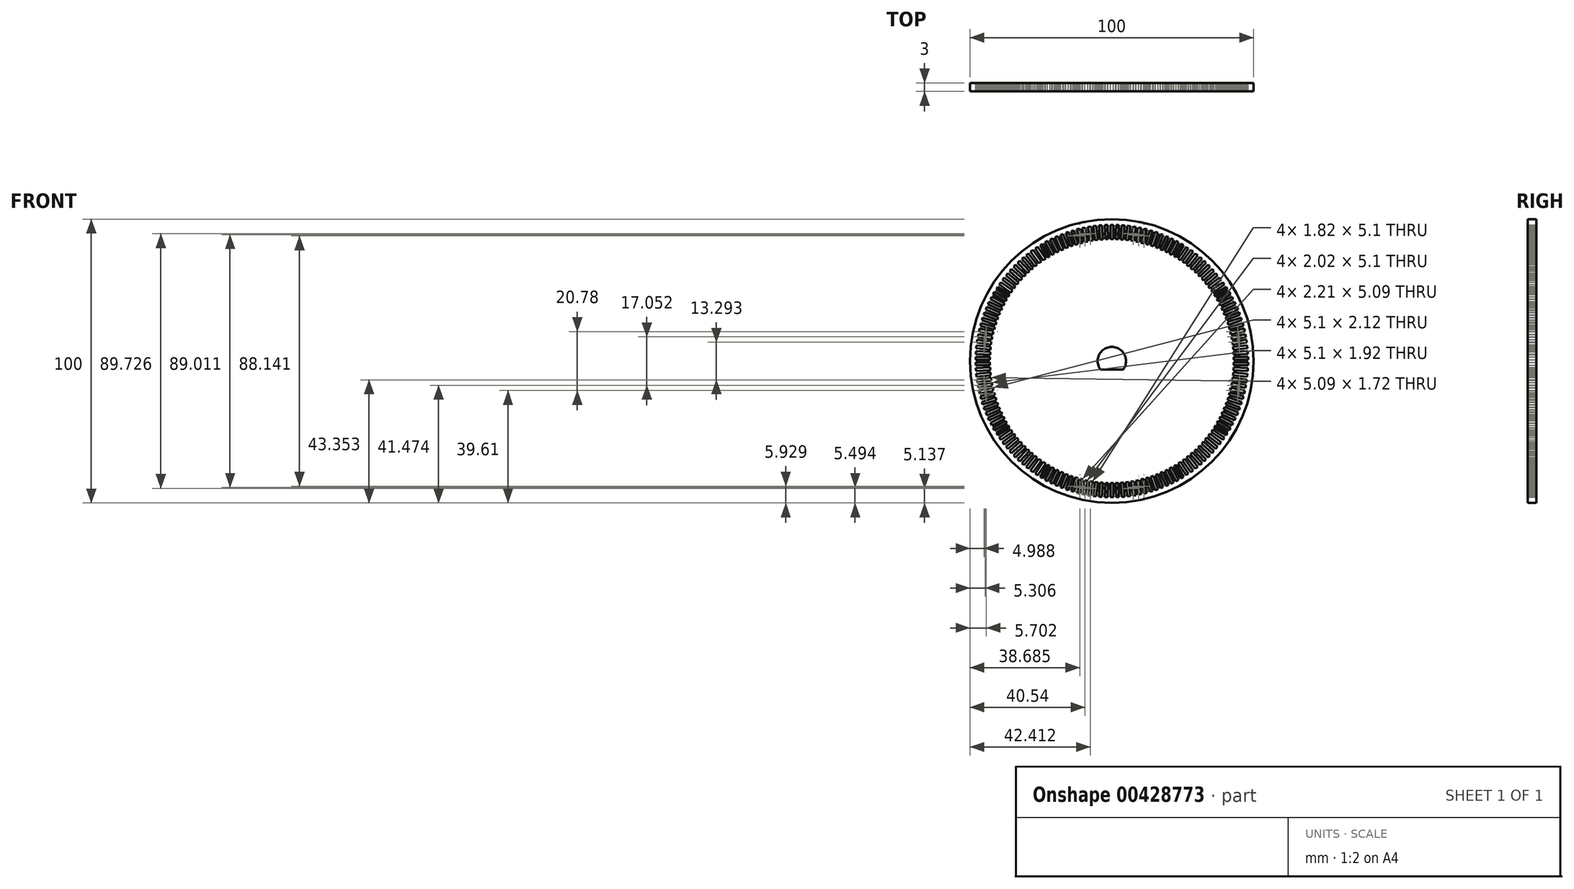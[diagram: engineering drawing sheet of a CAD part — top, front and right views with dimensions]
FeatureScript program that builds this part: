
annotation { "Feature Type Name" : "Feature", "Feature Type Description" : "" }
export const myFeature = defineFeature(function(context is Context, id is Id, definition is map)
    precondition{}
    {
        {
            var Q0;
            Q0=qCreatedBy(makeId("Front.planeOp"),FACE);
            var sketch = newSketch(context, id + "F0", { "sketchPlane" : qUnion([Q0])});
            skCircle(sketch, "E0", {"center": v(0, 0) * mm, "radius": 50 * mm});
            skLineSegment(sketch, "E1", {"start": v(0, 0) * mm, "end": v(0, 43) * mm});
            skLineSegment(sketch, "E2", {"start": v(0, 43) * mm, "end": v(0, 45.5) * mm});
            skLineSegment(sketch, "E3.bottom", {"start": v(0.5, 43) * mm, "end": v(-0.5, 43) * mm});
            skLineSegment(sketch, "E3.top", {"start": v(0.5, 48) * mm, "end": v(-0.5, 48) * mm});
            skLineSegment(sketch, "E3.left", {"start": v(0.5, 43) * mm, "end": v(0.5, 48) * mm});
            skLineSegment(sketch, "E3.right", {"start": v(-0.5, 43) * mm, "end": v(-0.5, 48) * mm});
            skPoint(sketch, "E3.middle", {"position": v(0, 45.5) * mm});
            skLineSegment(sketch, "E4.1.0", {"start": v(-2.3, 42.94) * mm, "end": v(-2.5, 47.94) * mm});
            skLineSegment(sketch, "E4.1.1", {"start": v(-1.3, 42.98) * mm, "end": v(-1.51, 47.98) * mm});
            skLineSegment(sketch, "E4.1.2", {"start": v(-1.8, 42.96) * mm, "end": v(-1.9, 45.46) * mm});
            skPoint(sketch, "E4.1.3", {"position": v(-1.9, 45.46) * mm});
            skLineSegment(sketch, "E4.1.4", {"start": v(-1.51, 47.98) * mm, "end": v(-2.5, 47.94) * mm});
            skLineSegment(sketch, "E4.1.5", {"start": v(-1.3, 42.98) * mm, "end": v(-2.3, 42.94) * mm});
            skLineSegment(sketch, "E4.2.0", {"start": v(-4.1, 42.8) * mm, "end": v(-4.51, 47.79) * mm});
            skLineSegment(sketch, "E4.2.1", {"start": v(-3.1, 42.9) * mm, "end": v(-3.52, 47.87) * mm});
            skLineSegment(sketch, "E4.2.2", {"start": v(-3.6, 42.85) * mm, "end": v(-3.8, 45.34) * mm});
            skPoint(sketch, "E4.2.3", {"position": v(-3.8, 45.34) * mm});
            skLineSegment(sketch, "E4.2.4", {"start": v(-3.52, 47.87) * mm, "end": v(-4.51, 47.79) * mm});
            skLineSegment(sketch, "E4.2.5", {"start": v(-3.1, 42.9) * mm, "end": v(-4.1, 42.8) * mm});
            skLineSegment(sketch, "E4.3.0", {"start": v(-5.89, 42.6) * mm, "end": v(-6.51, 47.56) * mm});
            skLineSegment(sketch, "E4.3.1", {"start": v(-4.9, 42.72) * mm, "end": v(-5.52, 47.68) * mm});
            skLineSegment(sketch, "E4.3.2", {"start": v(-5.39, 42.66) * mm, "end": v(-5.7, 45.14) * mm});
            skPoint(sketch, "E4.3.3", {"position": v(-5.7, 45.14) * mm});
            skLineSegment(sketch, "E4.3.4", {"start": v(-5.52, 47.68) * mm, "end": v(-6.51, 47.56) * mm});
            skLineSegment(sketch, "E4.3.5", {"start": v(-4.9, 42.72) * mm, "end": v(-5.89, 42.6) * mm});
            skLineSegment(sketch, "E4.4.0", {"start": v(-7.66, 42.31) * mm, "end": v(-8.5, 47.24) * mm});
            skLineSegment(sketch, "E4.4.1", {"start": v(-6.68, 42.48) * mm, "end": v(-7.51, 47.41) * mm});
            skLineSegment(sketch, "E4.4.2", {"start": v(-7.17, 42.4) * mm, "end": v(-7.59, 44.86) * mm});
            skPoint(sketch, "E4.4.3", {"position": v(-7.59, 44.86) * mm});
            skLineSegment(sketch, "E4.4.4", {"start": v(-7.51, 47.41) * mm, "end": v(-8.5, 47.24) * mm});
            skLineSegment(sketch, "E4.4.5", {"start": v(-6.68, 42.48) * mm, "end": v(-7.66, 42.31) * mm});
            skLineSegment(sketch, "E4.5.0", {"start": v(-9.43, 41.96) * mm, "end": v(-10.47, 46.85) * mm});
            skLineSegment(sketch, "E4.5.1", {"start": v(-8.45, 42.16) * mm, "end": v(-9.5, 47.06) * mm});
            skLineSegment(sketch, "E4.5.2", {"start": v(-8.94, 42.06) * mm, "end": v(-9.46, 44.5) * mm});
            skPoint(sketch, "E4.5.3", {"position": v(-9.46, 44.5) * mm});
            skLineSegment(sketch, "E4.5.4", {"start": v(-9.5, 47.06) * mm, "end": v(-10.47, 46.85) * mm});
            skLineSegment(sketch, "E4.5.5", {"start": v(-8.45, 42.16) * mm, "end": v(-9.43, 41.96) * mm});
            skLineSegment(sketch, "E4.6.0", {"start": v(-11.18, 41.52) * mm, "end": v(-12.42, 46.37) * mm});
            skLineSegment(sketch, "E4.6.1", {"start": v(-10.2, 41.77) * mm, "end": v(-11.45, 46.62) * mm});
            skLineSegment(sketch, "E4.6.2", {"start": v(-10.7, 41.65) * mm, "end": v(-11.32, 44.07) * mm});
            skPoint(sketch, "E4.6.3", {"position": v(-11.32, 44.07) * mm});
            skLineSegment(sketch, "E4.6.4", {"start": v(-11.45, 46.62) * mm, "end": v(-12.42, 46.37) * mm});
            skLineSegment(sketch, "E4.6.5", {"start": v(-10.2, 41.77) * mm, "end": v(-11.18, 41.52) * mm});
            skLineSegment(sketch, "E4.7.0", {"start": v(-12.9, 41.02) * mm, "end": v(-14.35, 45.8) * mm});
            skLineSegment(sketch, "E4.7.1", {"start": v(-11.95, 41.3) * mm, "end": v(-13.4, 46.1) * mm});
            skLineSegment(sketch, "E4.7.2", {"start": v(-12.43, 41.16) * mm, "end": v(-13.15, 43.56) * mm});
            skPoint(sketch, "E4.7.3", {"position": v(-13.15, 43.56) * mm});
            skLineSegment(sketch, "E4.7.4", {"start": v(-13.4, 46.1) * mm, "end": v(-14.35, 45.8) * mm});
            skLineSegment(sketch, "E4.7.5", {"start": v(-11.95, 41.3) * mm, "end": v(-12.9, 41.02) * mm});
            skLineSegment(sketch, "E4.8.0", {"start": v(-14.61, 40.44) * mm, "end": v(-16.26, 45.17) * mm});
            skLineSegment(sketch, "E4.8.1", {"start": v(-13.67, 40.77) * mm, "end": v(-15.31, 45.5) * mm});
            skLineSegment(sketch, "E4.8.2", {"start": v(-14.14, 40.6) * mm, "end": v(-14.96, 42.97) * mm});
            skPoint(sketch, "E4.8.3", {"position": v(-14.96, 42.97) * mm});
            skLineSegment(sketch, "E4.8.4", {"start": v(-15.31, 45.5) * mm, "end": v(-16.26, 45.17) * mm});
            skLineSegment(sketch, "E4.8.5", {"start": v(-13.67, 40.77) * mm, "end": v(-14.61, 40.44) * mm});
            skLineSegment(sketch, "E4.9.0", {"start": v(-16.3, 39.8) * mm, "end": v(-18.13, 44.45) * mm});
            skLineSegment(sketch, "E4.9.1", {"start": v(-15.36, 40.16) * mm, "end": v(-17.2, 44.81) * mm});
            skLineSegment(sketch, "E4.9.2", {"start": v(-15.83, 39.98) * mm, "end": v(-16.75, 42.3) * mm});
            skPoint(sketch, "E4.9.3", {"position": v(-16.75, 42.3) * mm});
            skLineSegment(sketch, "E4.9.4", {"start": v(-17.2, 44.81) * mm, "end": v(-18.13, 44.45) * mm});
            skLineSegment(sketch, "E4.9.5", {"start": v(-15.36, 40.16) * mm, "end": v(-16.3, 39.8) * mm});
            skLineSegment(sketch, "E4.10.0", {"start": v(-17.95, 39.08) * mm, "end": v(-19.98, 43.65) * mm});
            skLineSegment(sketch, "E4.10.1", {"start": v(-17.03, 39.49) * mm, "end": v(-19.07, 44.05) * mm});
            skLineSegment(sketch, "E4.10.2", {"start": v(-17.49, 39.28) * mm, "end": v(-18.5, 41.57) * mm});
            skPoint(sketch, "E4.10.3", {"position": v(-18.5, 41.57) * mm});
            skLineSegment(sketch, "E4.10.4", {"start": v(-19.07, 44.05) * mm, "end": v(-19.98, 43.65) * mm});
            skLineSegment(sketch, "E4.10.5", {"start": v(-17.03, 39.49) * mm, "end": v(-17.95, 39.08) * mm});
            skLineSegment(sketch, "E4.11.0", {"start": v(-19.57, 38.3) * mm, "end": v(-21.8, 42.77) * mm});
            skLineSegment(sketch, "E4.11.1", {"start": v(-18.67, 38.74) * mm, "end": v(-20.9, 43.22) * mm});
            skLineSegment(sketch, "E4.11.2", {"start": v(-19.12, 38.52) * mm, "end": v(-20.23, 40.75) * mm});
            skPoint(sketch, "E4.11.3", {"position": v(-20.23, 40.75) * mm});
            skLineSegment(sketch, "E4.11.4", {"start": v(-20.9, 43.22) * mm, "end": v(-21.8, 42.77) * mm});
            skLineSegment(sketch, "E4.11.5", {"start": v(-18.67, 38.74) * mm, "end": v(-19.57, 38.3) * mm});
            skLineSegment(sketch, "E4.12.0", {"start": v(-21.15, 37.44) * mm, "end": v(-23.56, 41.82) * mm});
            skLineSegment(sketch, "E4.12.1", {"start": v(-20.28, 37.92) * mm, "end": v(-22.69, 42.3) * mm});
            skLineSegment(sketch, "E4.12.2", {"start": v(-20.72, 37.68) * mm, "end": v(-21.92, 39.87) * mm});
            skPoint(sketch, "E4.12.3", {"position": v(-21.92, 39.87) * mm});
            skLineSegment(sketch, "E4.12.4", {"start": v(-22.69, 42.3) * mm, "end": v(-23.56, 41.82) * mm});
            skLineSegment(sketch, "E4.12.5", {"start": v(-20.28, 37.92) * mm, "end": v(-21.15, 37.44) * mm});
            skLineSegment(sketch, "E4.13.0", {"start": v(-22.7, 36.52) * mm, "end": v(-25.3, 40.8) * mm});
            skLineSegment(sketch, "E4.13.1", {"start": v(-21.85, 37.04) * mm, "end": v(-24.44, 41.32) * mm});
            skLineSegment(sketch, "E4.13.2", {"start": v(-22.28, 36.78) * mm, "end": v(-23.57, 38.92) * mm});
            skPoint(sketch, "E4.13.3", {"position": v(-23.57, 38.92) * mm});
            skLineSegment(sketch, "E4.13.4", {"start": v(-24.44, 41.32) * mm, "end": v(-25.3, 40.8) * mm});
            skLineSegment(sketch, "E4.13.5", {"start": v(-21.85, 37.04) * mm, "end": v(-22.7, 36.52) * mm});
            skLineSegment(sketch, "E4.14.0", {"start": v(-24.21, 35.54) * mm, "end": v(-26.98, 39.7) * mm});
            skLineSegment(sketch, "E4.14.1", {"start": v(-23.38, 36.1) * mm, "end": v(-26.15, 40.26) * mm});
            skLineSegment(sketch, "E4.14.2", {"start": v(-23.8, 35.82) * mm, "end": v(-25.18, 37.9) * mm});
            skPoint(sketch, "E4.14.3", {"position": v(-25.18, 37.9) * mm});
            skLineSegment(sketch, "E4.14.4", {"start": v(-26.15, 40.26) * mm, "end": v(-26.98, 39.7) * mm});
            skLineSegment(sketch, "E4.14.5", {"start": v(-23.38, 36.1) * mm, "end": v(-24.21, 35.54) * mm});
            skLineSegment(sketch, "E4.15.0", {"start": v(-25.68, 34.5) * mm, "end": v(-28.62, 38.54) * mm});
            skLineSegment(sketch, "E4.15.1", {"start": v(-24.87, 35.08) * mm, "end": v(-27.8, 39.13) * mm});
            skLineSegment(sketch, "E4.15.2", {"start": v(-25.27, 34.79) * mm, "end": v(-26.74, 36.81) * mm});
            skPoint(sketch, "E4.15.3", {"position": v(-26.74, 36.81) * mm});
            skLineSegment(sketch, "E4.15.4", {"start": v(-27.8, 39.13) * mm, "end": v(-28.62, 38.54) * mm});
            skLineSegment(sketch, "E4.15.5", {"start": v(-24.87, 35.08) * mm, "end": v(-25.68, 34.5) * mm});
            skLineSegment(sketch, "E4.16.0", {"start": v(-27.1, 33.39) * mm, "end": v(-30.2, 37.3) * mm});
            skLineSegment(sketch, "E4.16.1", {"start": v(-26.32, 34) * mm, "end": v(-29.42, 37.93) * mm});
            skLineSegment(sketch, "E4.16.2", {"start": v(-26.7, 33.7) * mm, "end": v(-28.26, 35.66) * mm});
            skPoint(sketch, "E4.16.3", {"position": v(-28.26, 35.66) * mm});
            skLineSegment(sketch, "E4.16.4", {"start": v(-29.42, 37.93) * mm, "end": v(-30.2, 37.3) * mm});
            skLineSegment(sketch, "E4.16.5", {"start": v(-26.32, 34) * mm, "end": v(-27.1, 33.39) * mm});
            skLineSegment(sketch, "E4.17.0", {"start": v(-28.48, 32.22) * mm, "end": v(-31.74, 36) * mm});
            skLineSegment(sketch, "E4.17.1", {"start": v(-27.72, 32.88) * mm, "end": v(-30.99, 36.66) * mm});
            skLineSegment(sketch, "E4.17.2", {"start": v(-28.1, 32.55) * mm, "end": v(-29.73, 34.44) * mm});
            skPoint(sketch, "E4.17.3", {"position": v(-29.73, 34.44) * mm});
            skLineSegment(sketch, "E4.17.4", {"start": v(-30.99, 36.66) * mm, "end": v(-31.74, 36) * mm});
            skLineSegment(sketch, "E4.17.5", {"start": v(-27.72, 32.88) * mm, "end": v(-28.48, 32.22) * mm});
            skLineSegment(sketch, "E4.18.0", {"start": v(-29.8, 31) * mm, "end": v(-33.22, 34.65) * mm});
            skLineSegment(sketch, "E4.18.1", {"start": v(-29.07, 31.69) * mm, "end": v(-32.5, 35.33) * mm});
            skLineSegment(sketch, "E4.18.2", {"start": v(-29.44, 31.35) * mm, "end": v(-31.15, 33.17) * mm});
            skPoint(sketch, "E4.18.3", {"position": v(-31.15, 33.17) * mm});
            skLineSegment(sketch, "E4.18.4", {"start": v(-32.5, 35.33) * mm, "end": v(-33.22, 34.65) * mm});
            skLineSegment(sketch, "E4.18.5", {"start": v(-29.07, 31.69) * mm, "end": v(-29.8, 31) * mm});
            skLineSegment(sketch, "E4.19.0", {"start": v(-31.07, 29.73) * mm, "end": v(-34.64, 33.23) * mm});
            skLineSegment(sketch, "E4.19.1", {"start": v(-30.37, 30.44) * mm, "end": v(-33.94, 33.94) * mm});
            skLineSegment(sketch, "E4.19.2", {"start": v(-30.72, 30.09) * mm, "end": v(-32.5, 31.83) * mm});
            skPoint(sketch, "E4.19.3", {"position": v(-32.5, 31.83) * mm});
            skLineSegment(sketch, "E4.19.4", {"start": v(-33.94, 33.94) * mm, "end": v(-34.64, 33.23) * mm});
            skLineSegment(sketch, "E4.19.5", {"start": v(-30.37, 30.44) * mm, "end": v(-31.07, 29.73) * mm});
            skLineSegment(sketch, "E5.1.20.0", {"start": v(-32.29, 28.4) * mm, "end": v(-36, 31.75) * mm});
            skLineSegment(sketch, "E5.3.20.0", {"start": v(-31.62, 29.14) * mm, "end": v(-35.34, 32.49) * mm});
            skLineSegment(sketch, "E5.6.20.0", {"start": v(-31.96, 28.77) * mm, "end": v(-33.81, 30.45) * mm});
            skPoint(sketch, "E5.9.20.0", {"position": v(-33.81, 30.45) * mm});
            skLineSegment(sketch, "E5.10.20.0", {"start": v(-35.34, 32.49) * mm, "end": v(-36, 31.75) * mm});
            skLineSegment(sketch, "E5.13.20.0", {"start": v(-31.62, 29.14) * mm, "end": v(-32.29, 28.4) * mm});
            skLineSegment(sketch, "E5.1.21.0", {"start": v(-33.45, 27.02) * mm, "end": v(-37.3, 30.21) * mm});
            skLineSegment(sketch, "E5.3.21.0", {"start": v(-32.81, 27.8) * mm, "end": v(-36.67, 30.98) * mm});
            skLineSegment(sketch, "E5.6.21.0", {"start": v(-33.13, 27.4) * mm, "end": v(-35.06, 29) * mm});
            skPoint(sketch, "E5.9.21.0", {"position": v(-35.06, 29) * mm});
            skLineSegment(sketch, "E5.10.21.0", {"start": v(-36.67, 30.98) * mm, "end": v(-37.3, 30.21) * mm});
            skLineSegment(sketch, "E5.13.21.0", {"start": v(-32.81, 27.8) * mm, "end": v(-33.45, 27.02) * mm});
            skLineSegment(sketch, "E5.1.22.0", {"start": v(-34.55, 25.6) * mm, "end": v(-38.54, 28.62) * mm});
            skLineSegment(sketch, "E5.3.22.0", {"start": v(-33.95, 26.4) * mm, "end": v(-37.93, 29.42) * mm});
            skLineSegment(sketch, "E5.6.22.0", {"start": v(-34.25, 26) * mm, "end": v(-36.24, 27.5) * mm});
            skPoint(sketch, "E5.9.22.0", {"position": v(-36.24, 27.5) * mm});
            skLineSegment(sketch, "E5.10.22.0", {"start": v(-37.93, 29.42) * mm, "end": v(-38.54, 28.62) * mm});
            skLineSegment(sketch, "E5.13.22.0", {"start": v(-33.95, 26.4) * mm, "end": v(-34.55, 25.6) * mm});
            skLineSegment(sketch, "E5.1.23.0", {"start": v(-35.6, 24.13) * mm, "end": v(-39.7, 26.98) * mm});
            skLineSegment(sketch, "E5.3.23.0", {"start": v(-35.02, 24.95) * mm, "end": v(-39.13, 27.8) * mm});
            skLineSegment(sketch, "E5.6.23.0", {"start": v(-35.3, 24.54) * mm, "end": v(-37.36, 25.97) * mm});
            skPoint(sketch, "E5.9.23.0", {"position": v(-37.36, 25.97) * mm});
            skLineSegment(sketch, "E5.10.23.0", {"start": v(-39.13, 27.8) * mm, "end": v(-39.7, 26.98) * mm});
            skLineSegment(sketch, "E5.13.23.0", {"start": v(-35.02, 24.95) * mm, "end": v(-35.6, 24.13) * mm});
            skLineSegment(sketch, "E5.1.24.0", {"start": v(-36.57, 22.62) * mm, "end": v(-40.8, 25.3) * mm});
            skLineSegment(sketch, "E5.3.24.0", {"start": v(-36.04, 23.46) * mm, "end": v(-40.26, 26.14) * mm});
            skLineSegment(sketch, "E5.6.24.0", {"start": v(-36.3, 23.04) * mm, "end": v(-38.42, 24.38) * mm});
            skPoint(sketch, "E5.9.24.0", {"position": v(-38.42, 24.38) * mm});
            skLineSegment(sketch, "E5.10.24.0", {"start": v(-40.26, 26.14) * mm, "end": v(-40.8, 25.3) * mm});
            skLineSegment(sketch, "E5.13.24.0", {"start": v(-36.04, 23.46) * mm, "end": v(-36.57, 22.62) * mm});
            skLineSegment(sketch, "E5.1.25.0", {"start": v(-37.49, 21.07) * mm, "end": v(-41.82, 23.57) * mm});
            skLineSegment(sketch, "E5.3.25.0", {"start": v(-36.99, 21.93) * mm, "end": v(-41.32, 24.43) * mm});
            skLineSegment(sketch, "E5.6.25.0", {"start": v(-37.24, 21.5) * mm, "end": v(-39.4, 22.75) * mm});
            skPoint(sketch, "E5.9.25.0", {"position": v(-39.4, 22.75) * mm});
            skLineSegment(sketch, "E5.10.25.0", {"start": v(-41.32, 24.43) * mm, "end": v(-41.82, 23.57) * mm});
            skLineSegment(sketch, "E5.13.25.0", {"start": v(-36.99, 21.93) * mm, "end": v(-37.49, 21.07) * mm});
            skLineSegment(sketch, "E5.1.26.0", {"start": v(-38.34, 19.48) * mm, "end": v(-42.77, 21.8) * mm});
            skLineSegment(sketch, "E5.3.26.0", {"start": v(-37.88, 20.36) * mm, "end": v(-42.3, 22.68) * mm});
            skLineSegment(sketch, "E5.6.26.0", {"start": v(-38.1, 19.92) * mm, "end": v(-40.32, 21.08) * mm});
            skPoint(sketch, "E5.9.26.0", {"position": v(-40.32, 21.08) * mm});
            skLineSegment(sketch, "E5.10.26.0", {"start": v(-42.3, 22.68) * mm, "end": v(-42.77, 21.8) * mm});
            skLineSegment(sketch, "E5.13.26.0", {"start": v(-37.88, 20.36) * mm, "end": v(-38.34, 19.48) * mm});
            skLineSegment(sketch, "E5.1.27.0", {"start": v(-39.12, 17.86) * mm, "end": v(-43.64, 19.98) * mm});
            skLineSegment(sketch, "E5.3.27.0", {"start": v(-38.7, 18.76) * mm, "end": v(-43.22, 20.89) * mm});
            skLineSegment(sketch, "E5.6.27.0", {"start": v(-38.9, 18.3) * mm, "end": v(-41.17, 19.37) * mm});
            skPoint(sketch, "E5.9.27.0", {"position": v(-41.17, 19.37) * mm});
            skLineSegment(sketch, "E5.10.27.0", {"start": v(-43.22, 20.89) * mm, "end": v(-43.64, 19.98) * mm});
            skLineSegment(sketch, "E5.13.27.0", {"start": v(-38.7, 18.76) * mm, "end": v(-39.12, 17.86) * mm});
            skLineSegment(sketch, "E5.1.28.0", {"start": v(-39.83, 16.2) * mm, "end": v(-44.44, 18.14) * mm});
            skLineSegment(sketch, "E5.3.28.0", {"start": v(-39.45, 17.12) * mm, "end": v(-44.06, 19.06) * mm});
            skLineSegment(sketch, "E5.6.28.0", {"start": v(-39.64, 16.66) * mm, "end": v(-41.94, 17.63) * mm});
            skPoint(sketch, "E5.9.28.0", {"position": v(-41.94, 17.63) * mm});
            skLineSegment(sketch, "E5.10.28.0", {"start": v(-44.06, 19.06) * mm, "end": v(-44.44, 18.14) * mm});
            skLineSegment(sketch, "E5.13.28.0", {"start": v(-39.45, 17.12) * mm, "end": v(-39.83, 16.2) * mm});
            skLineSegment(sketch, "E5.1.29.0", {"start": v(-40.48, 14.52) * mm, "end": v(-45.16, 16.26) * mm});
            skLineSegment(sketch, "E5.3.29.0", {"start": v(-40.13, 15.46) * mm, "end": v(-44.82, 17.2) * mm});
            skLineSegment(sketch, "E5.6.29.0", {"start": v(-40.3, 14.99) * mm, "end": v(-42.65, 15.86) * mm});
            skPoint(sketch, "E5.9.29.0", {"position": v(-42.65, 15.86) * mm});
            skLineSegment(sketch, "E5.10.29.0", {"start": v(-44.82, 17.2) * mm, "end": v(-45.16, 16.26) * mm});
            skLineSegment(sketch, "E5.13.29.0", {"start": v(-40.13, 15.46) * mm, "end": v(-40.48, 14.52) * mm});
            skLineSegment(sketch, "E5.1.30.0", {"start": v(-41.05, 12.81) * mm, "end": v(-45.8, 14.36) * mm});
            skLineSegment(sketch, "E5.3.30.0", {"start": v(-40.74, 13.76) * mm, "end": v(-45.5, 15.3) * mm});
            skLineSegment(sketch, "E5.6.30.0", {"start": v(-40.9, 13.29) * mm, "end": v(-43.27, 14.06) * mm});
            skPoint(sketch, "E5.9.30.0", {"position": v(-43.27, 14.06) * mm});
            skLineSegment(sketch, "E5.10.30.0", {"start": v(-45.5, 15.3) * mm, "end": v(-45.8, 14.36) * mm});
            skLineSegment(sketch, "E5.13.30.0", {"start": v(-40.74, 13.76) * mm, "end": v(-41.05, 12.81) * mm});
            skLineSegment(sketch, "E5.1.31.0", {"start": v(-41.55, 11.08) * mm, "end": v(-46.37, 12.43) * mm});
            skLineSegment(sketch, "E5.3.31.0", {"start": v(-41.28, 12.05) * mm, "end": v(-46.1, 13.39) * mm});
            skLineSegment(sketch, "E5.6.31.0", {"start": v(-41.42, 11.56) * mm, "end": v(-43.82, 12.24) * mm});
            skPoint(sketch, "E5.9.31.0", {"position": v(-43.82, 12.24) * mm});
            skLineSegment(sketch, "E5.10.31.0", {"start": v(-46.1, 13.39) * mm, "end": v(-46.37, 12.43) * mm});
            skLineSegment(sketch, "E5.13.31.0", {"start": v(-41.28, 12.05) * mm, "end": v(-41.55, 11.08) * mm});
            skLineSegment(sketch, "E5.1.32.0", {"start": v(-41.98, 9.33) * mm, "end": v(-46.85, 10.47) * mm});
            skLineSegment(sketch, "E5.3.32.0", {"start": v(-41.75, 10.3) * mm, "end": v(-46.62, 11.45) * mm});
            skLineSegment(sketch, "E5.6.32.0", {"start": v(-41.86, 9.82) * mm, "end": v(-44.3, 10.39) * mm});
            skPoint(sketch, "E5.9.32.0", {"position": v(-44.3, 10.39) * mm});
            skLineSegment(sketch, "E5.10.32.0", {"start": v(-46.62, 11.45) * mm, "end": v(-46.85, 10.47) * mm});
            skLineSegment(sketch, "E5.13.32.0", {"start": v(-41.75, 10.3) * mm, "end": v(-41.98, 9.33) * mm});
            skLineSegment(sketch, "E5.1.33.0", {"start": v(-42.33, 7.57) * mm, "end": v(-47.24, 8.5) * mm});
            skLineSegment(sketch, "E5.3.33.0", {"start": v(-42.14, 8.55) * mm, "end": v(-47.06, 9.49) * mm});
            skLineSegment(sketch, "E5.6.33.0", {"start": v(-42.24, 8.06) * mm, "end": v(-44.7, 8.53) * mm});
            skPoint(sketch, "E5.9.33.0", {"position": v(-44.7, 8.53) * mm});
            skLineSegment(sketch, "E5.10.33.0", {"start": v(-47.06, 9.49) * mm, "end": v(-47.24, 8.5) * mm});
            skLineSegment(sketch, "E5.13.33.0", {"start": v(-42.14, 8.55) * mm, "end": v(-42.33, 7.57) * mm});
            skLineSegment(sketch, "E5.1.34.0", {"start": v(-42.61, 5.79) * mm, "end": v(-47.56, 6.52) * mm});
            skLineSegment(sketch, "E5.3.34.0", {"start": v(-42.47, 6.78) * mm, "end": v(-47.41, 7.5) * mm});
            skLineSegment(sketch, "E5.6.34.0", {"start": v(-42.54, 6.28) * mm, "end": v(-45.01, 6.65) * mm});
            skPoint(sketch, "E5.9.34.0", {"position": v(-45.01, 6.65) * mm});
            skLineSegment(sketch, "E5.10.34.0", {"start": v(-47.41, 7.5) * mm, "end": v(-47.56, 6.52) * mm});
            skLineSegment(sketch, "E5.13.34.0", {"start": v(-42.47, 6.78) * mm, "end": v(-42.61, 5.79) * mm});
            skLineSegment(sketch, "E5.1.35.0", {"start": v(-42.82, 4) * mm, "end": v(-47.79, 4.52) * mm});
            skLineSegment(sketch, "E5.3.35.0", {"start": v(-42.71, 5) * mm, "end": v(-47.68, 5.51) * mm});
            skLineSegment(sketch, "E5.6.35.0", {"start": v(-42.76, 4.5) * mm, "end": v(-45.25, 4.76) * mm});
            skPoint(sketch, "E5.9.35.0", {"position": v(-45.25, 4.76) * mm});
            skLineSegment(sketch, "E5.10.35.0", {"start": v(-47.68, 5.51) * mm, "end": v(-47.79, 4.52) * mm});
            skLineSegment(sketch, "E5.13.35.0", {"start": v(-42.71, 5) * mm, "end": v(-42.82, 4) * mm});
            skLineSegment(sketch, "E5.1.36.0", {"start": v(-42.95, 2.2) * mm, "end": v(-47.94, 2.51) * mm});
            skLineSegment(sketch, "E5.3.36.0", {"start": v(-42.88, 3.2) * mm, "end": v(-47.87, 3.51) * mm});
            skLineSegment(sketch, "E5.6.36.0", {"start": v(-42.92, 2.7) * mm, "end": v(-45.41, 2.86) * mm});
            skPoint(sketch, "E5.9.36.0", {"position": v(-45.41, 2.86) * mm});
            skLineSegment(sketch, "E5.10.36.0", {"start": v(-47.87, 3.51) * mm, "end": v(-47.94, 2.51) * mm});
            skLineSegment(sketch, "E5.13.36.0", {"start": v(-42.88, 3.2) * mm, "end": v(-42.95, 2.2) * mm});
            skLineSegment(sketch, "E5.1.37.0", {"start": v(-43, 0.4) * mm, "end": v(-48, 0.5) * mm});
            skLineSegment(sketch, "E5.3.37.0", {"start": v(-42.98, 1.4) * mm, "end": v(-47.98, 1.5) * mm});
            skLineSegment(sketch, "E5.6.37.0", {"start": v(-43, 0.9) * mm, "end": v(-45.5, 0.95) * mm});
            skPoint(sketch, "E5.9.37.0", {"position": v(-45.5, 0.95) * mm});
            skLineSegment(sketch, "E5.10.37.0", {"start": v(-47.98, 1.5) * mm, "end": v(-48, 0.5) * mm});
            skLineSegment(sketch, "E5.13.37.0", {"start": v(-42.98, 1.4) * mm, "end": v(-43, 0.4) * mm});
            skLineSegment(sketch, "E5.1.38.0", {"start": v(-42.98, -1.4) * mm, "end": v(-47.98, -1.5) * mm});
            skLineSegment(sketch, "E5.3.38.0", {"start": v(-43, -0.4) * mm, "end": v(-48, -0.5) * mm});
            skLineSegment(sketch, "E5.6.38.0", {"start": v(-43, -0.9) * mm, "end": v(-45.5, -0.95) * mm});
            skPoint(sketch, "E5.9.38.0", {"position": v(-45.5, -0.95) * mm});
            skLineSegment(sketch, "E5.10.38.0", {"start": v(-48, -0.5) * mm, "end": v(-47.98, -1.5) * mm});
            skLineSegment(sketch, "E5.13.38.0", {"start": v(-43, -0.4) * mm, "end": v(-42.98, -1.4) * mm});
            skLineSegment(sketch, "E5.1.39.0", {"start": v(-42.88, -3.2) * mm, "end": v(-47.87, -3.51) * mm});
            skLineSegment(sketch, "E5.3.39.0", {"start": v(-42.95, -2.2) * mm, "end": v(-47.94, -2.51) * mm});
            skLineSegment(sketch, "E5.6.39.0", {"start": v(-42.92, -2.7) * mm, "end": v(-45.41, -2.86) * mm});
            skPoint(sketch, "E5.9.39.0", {"position": v(-45.41, -2.86) * mm});
            skLineSegment(sketch, "E5.10.39.0", {"start": v(-47.94, -2.51) * mm, "end": v(-47.87, -3.51) * mm});
            skLineSegment(sketch, "E5.13.39.0", {"start": v(-42.95, -2.2) * mm, "end": v(-42.88, -3.2) * mm});
            skArc(sketch, "E6", {"start": v(4, -3) * mm, "mid": v(0, 5) * mm, "end": v(-4, -3) * mm});
            skLineSegment(sketch, "E7", {"start": v(0, 5) * mm, "end": v(0, -3) * mm, "construction": true});
            skLineSegment(sketch, "E8", {"start": v(-4, -3) * mm, "end": v(4, -3) * mm});
            skLineSegment(sketch, "E9.1.40.0", {"start": v(-42.71, -5) * mm, "end": v(-47.68, -5.51) * mm});
            skLineSegment(sketch, "E9.3.40.0", {"start": v(-42.82, -4) * mm, "end": v(-47.79, -4.52) * mm});
            skLineSegment(sketch, "E9.6.40.0", {"start": v(-42.76, -4.5) * mm, "end": v(-45.25, -4.76) * mm});
            skPoint(sketch, "E9.9.40.0", {"position": v(-45.25, -4.76) * mm});
            skLineSegment(sketch, "E9.10.40.0", {"start": v(-47.79, -4.52) * mm, "end": v(-47.68, -5.51) * mm});
            skLineSegment(sketch, "E9.13.40.0", {"start": v(-42.82, -4) * mm, "end": v(-42.71, -5) * mm});
            skLineSegment(sketch, "E9.1.41.0", {"start": v(-42.47, -6.78) * mm, "end": v(-47.41, -7.5) * mm});
            skLineSegment(sketch, "E9.3.41.0", {"start": v(-42.61, -5.79) * mm, "end": v(-47.56, -6.52) * mm});
            skLineSegment(sketch, "E9.6.41.0", {"start": v(-42.54, -6.28) * mm, "end": v(-45.01, -6.65) * mm});
            skPoint(sketch, "E9.9.41.0", {"position": v(-45.01, -6.65) * mm});
            skLineSegment(sketch, "E9.10.41.0", {"start": v(-47.56, -6.52) * mm, "end": v(-47.41, -7.5) * mm});
            skLineSegment(sketch, "E9.13.41.0", {"start": v(-42.61, -5.79) * mm, "end": v(-42.47, -6.78) * mm});
            skLineSegment(sketch, "E9.1.42.0", {"start": v(-42.14, -8.55) * mm, "end": v(-47.06, -9.49) * mm});
            skLineSegment(sketch, "E9.3.42.0", {"start": v(-42.33, -7.57) * mm, "end": v(-47.24, -8.5) * mm});
            skLineSegment(sketch, "E9.6.42.0", {"start": v(-42.24, -8.06) * mm, "end": v(-44.7, -8.53) * mm});
            skPoint(sketch, "E9.9.42.0", {"position": v(-44.7, -8.53) * mm});
            skLineSegment(sketch, "E9.10.42.0", {"start": v(-47.24, -8.5) * mm, "end": v(-47.06, -9.49) * mm});
            skLineSegment(sketch, "E9.13.42.0", {"start": v(-42.33, -7.57) * mm, "end": v(-42.14, -8.55) * mm});
            skLineSegment(sketch, "E9.1.43.0", {"start": v(-41.75, -10.3) * mm, "end": v(-46.62, -11.45) * mm});
            skLineSegment(sketch, "E9.3.43.0", {"start": v(-41.98, -9.33) * mm, "end": v(-46.85, -10.47) * mm});
            skLineSegment(sketch, "E9.6.43.0", {"start": v(-41.86, -9.82) * mm, "end": v(-44.3, -10.39) * mm});
            skPoint(sketch, "E9.9.43.0", {"position": v(-44.3, -10.39) * mm});
            skLineSegment(sketch, "E9.10.43.0", {"start": v(-46.85, -10.47) * mm, "end": v(-46.62, -11.45) * mm});
            skLineSegment(sketch, "E9.13.43.0", {"start": v(-41.98, -9.33) * mm, "end": v(-41.75, -10.3) * mm});
            skLineSegment(sketch, "E9.1.44.0", {"start": v(-41.28, -12.05) * mm, "end": v(-46.1, -13.39) * mm});
            skLineSegment(sketch, "E9.3.44.0", {"start": v(-41.55, -11.08) * mm, "end": v(-46.37, -12.43) * mm});
            skLineSegment(sketch, "E9.6.44.0", {"start": v(-41.42, -11.56) * mm, "end": v(-43.82, -12.24) * mm});
            skPoint(sketch, "E9.9.44.0", {"position": v(-43.82, -12.24) * mm});
            skLineSegment(sketch, "E9.10.44.0", {"start": v(-46.37, -12.43) * mm, "end": v(-46.1, -13.39) * mm});
            skLineSegment(sketch, "E9.13.44.0", {"start": v(-41.55, -11.08) * mm, "end": v(-41.28, -12.05) * mm});
            skLineSegment(sketch, "E9.1.45.0", {"start": v(-40.74, -13.76) * mm, "end": v(-45.5, -15.3) * mm});
            skLineSegment(sketch, "E9.3.45.0", {"start": v(-41.05, -12.81) * mm, "end": v(-45.8, -14.36) * mm});
            skLineSegment(sketch, "E9.6.45.0", {"start": v(-40.9, -13.29) * mm, "end": v(-43.27, -14.06) * mm});
            skPoint(sketch, "E9.9.45.0", {"position": v(-43.27, -14.06) * mm});
            skLineSegment(sketch, "E9.10.45.0", {"start": v(-45.8, -14.36) * mm, "end": v(-45.5, -15.3) * mm});
            skLineSegment(sketch, "E9.13.45.0", {"start": v(-41.05, -12.81) * mm, "end": v(-40.74, -13.76) * mm});
            skLineSegment(sketch, "E9.1.46.0", {"start": v(-40.13, -15.46) * mm, "end": v(-44.82, -17.2) * mm});
            skLineSegment(sketch, "E9.3.46.0", {"start": v(-40.48, -14.52) * mm, "end": v(-45.16, -16.26) * mm});
            skLineSegment(sketch, "E9.6.46.0", {"start": v(-40.3, -14.99) * mm, "end": v(-42.65, -15.86) * mm});
            skPoint(sketch, "E9.9.46.0", {"position": v(-42.65, -15.86) * mm});
            skLineSegment(sketch, "E9.10.46.0", {"start": v(-45.16, -16.26) * mm, "end": v(-44.82, -17.2) * mm});
            skLineSegment(sketch, "E9.13.46.0", {"start": v(-40.48, -14.52) * mm, "end": v(-40.13, -15.46) * mm});
            skLineSegment(sketch, "E9.1.47.0", {"start": v(-39.45, -17.12) * mm, "end": v(-44.06, -19.06) * mm});
            skLineSegment(sketch, "E9.3.47.0", {"start": v(-39.83, -16.2) * mm, "end": v(-44.44, -18.14) * mm});
            skLineSegment(sketch, "E9.6.47.0", {"start": v(-39.64, -16.66) * mm, "end": v(-41.94, -17.63) * mm});
            skPoint(sketch, "E9.9.47.0", {"position": v(-41.94, -17.63) * mm});
            skLineSegment(sketch, "E9.10.47.0", {"start": v(-44.44, -18.14) * mm, "end": v(-44.06, -19.06) * mm});
            skLineSegment(sketch, "E9.13.47.0", {"start": v(-39.83, -16.2) * mm, "end": v(-39.45, -17.12) * mm});
            skLineSegment(sketch, "E9.1.48.0", {"start": v(-38.7, -18.76) * mm, "end": v(-43.22, -20.89) * mm});
            skLineSegment(sketch, "E9.3.48.0", {"start": v(-39.12, -17.86) * mm, "end": v(-43.64, -19.98) * mm});
            skLineSegment(sketch, "E9.6.48.0", {"start": v(-38.9, -18.3) * mm, "end": v(-41.17, -19.37) * mm});
            skPoint(sketch, "E9.9.48.0", {"position": v(-41.17, -19.37) * mm});
            skLineSegment(sketch, "E9.10.48.0", {"start": v(-43.64, -19.98) * mm, "end": v(-43.22, -20.89) * mm});
            skLineSegment(sketch, "E9.13.48.0", {"start": v(-39.12, -17.86) * mm, "end": v(-38.7, -18.76) * mm});
            skLineSegment(sketch, "E9.1.49.0", {"start": v(-37.88, -20.36) * mm, "end": v(-42.3, -22.68) * mm});
            skLineSegment(sketch, "E9.3.49.0", {"start": v(-38.34, -19.48) * mm, "end": v(-42.77, -21.8) * mm});
            skLineSegment(sketch, "E9.6.49.0", {"start": v(-38.1, -19.92) * mm, "end": v(-40.32, -21.08) * mm});
            skPoint(sketch, "E9.9.49.0", {"position": v(-40.32, -21.08) * mm});
            skLineSegment(sketch, "E9.10.49.0", {"start": v(-42.77, -21.8) * mm, "end": v(-42.3, -22.68) * mm});
            skLineSegment(sketch, "E9.13.49.0", {"start": v(-38.34, -19.48) * mm, "end": v(-37.88, -20.36) * mm});
            skLineSegment(sketch, "E9.1.50.0", {"start": v(-36.99, -21.93) * mm, "end": v(-41.32, -24.43) * mm});
            skLineSegment(sketch, "E9.3.50.0", {"start": v(-37.49, -21.07) * mm, "end": v(-41.82, -23.57) * mm});
            skLineSegment(sketch, "E9.6.50.0", {"start": v(-37.24, -21.5) * mm, "end": v(-39.4, -22.75) * mm});
            skPoint(sketch, "E9.9.50.0", {"position": v(-39.4, -22.75) * mm});
            skLineSegment(sketch, "E9.10.50.0", {"start": v(-41.82, -23.57) * mm, "end": v(-41.32, -24.43) * mm});
            skLineSegment(sketch, "E9.13.50.0", {"start": v(-37.49, -21.07) * mm, "end": v(-36.99, -21.93) * mm});
            skLineSegment(sketch, "E9.1.51.0", {"start": v(-36.04, -23.46) * mm, "end": v(-40.26, -26.14) * mm});
            skLineSegment(sketch, "E9.3.51.0", {"start": v(-36.57, -22.62) * mm, "end": v(-40.8, -25.3) * mm});
            skLineSegment(sketch, "E9.6.51.0", {"start": v(-36.3, -23.04) * mm, "end": v(-38.42, -24.38) * mm});
            skPoint(sketch, "E9.9.51.0", {"position": v(-38.42, -24.38) * mm});
            skLineSegment(sketch, "E9.10.51.0", {"start": v(-40.8, -25.3) * mm, "end": v(-40.26, -26.14) * mm});
            skLineSegment(sketch, "E9.13.51.0", {"start": v(-36.57, -22.62) * mm, "end": v(-36.04, -23.46) * mm});
            skLineSegment(sketch, "E9.1.52.0", {"start": v(-35.02, -24.95) * mm, "end": v(-39.13, -27.8) * mm});
            skLineSegment(sketch, "E9.3.52.0", {"start": v(-35.6, -24.13) * mm, "end": v(-39.7, -26.98) * mm});
            skLineSegment(sketch, "E9.6.52.0", {"start": v(-35.3, -24.54) * mm, "end": v(-37.36, -25.97) * mm});
            skPoint(sketch, "E9.9.52.0", {"position": v(-37.36, -25.97) * mm});
            skLineSegment(sketch, "E9.10.52.0", {"start": v(-39.7, -26.98) * mm, "end": v(-39.13, -27.8) * mm});
            skLineSegment(sketch, "E9.13.52.0", {"start": v(-35.6, -24.13) * mm, "end": v(-35.02, -24.95) * mm});
            skLineSegment(sketch, "E9.1.53.0", {"start": v(-33.95, -26.4) * mm, "end": v(-37.93, -29.42) * mm});
            skLineSegment(sketch, "E9.3.53.0", {"start": v(-34.55, -25.6) * mm, "end": v(-38.54, -28.62) * mm});
            skLineSegment(sketch, "E9.6.53.0", {"start": v(-34.25, -26) * mm, "end": v(-36.24, -27.5) * mm});
            skPoint(sketch, "E9.9.53.0", {"position": v(-36.24, -27.5) * mm});
            skLineSegment(sketch, "E9.10.53.0", {"start": v(-38.54, -28.62) * mm, "end": v(-37.93, -29.42) * mm});
            skLineSegment(sketch, "E9.13.53.0", {"start": v(-34.55, -25.6) * mm, "end": v(-33.95, -26.4) * mm});
            skLineSegment(sketch, "E9.1.54.0", {"start": v(-32.81, -27.8) * mm, "end": v(-36.67, -30.98) * mm});
            skLineSegment(sketch, "E9.3.54.0", {"start": v(-33.45, -27.02) * mm, "end": v(-37.3, -30.21) * mm});
            skLineSegment(sketch, "E9.6.54.0", {"start": v(-33.13, -27.4) * mm, "end": v(-35.06, -29) * mm});
            skPoint(sketch, "E9.9.54.0", {"position": v(-35.06, -29) * mm});
            skLineSegment(sketch, "E9.10.54.0", {"start": v(-37.3, -30.21) * mm, "end": v(-36.67, -30.98) * mm});
            skLineSegment(sketch, "E9.13.54.0", {"start": v(-33.45, -27.02) * mm, "end": v(-32.81, -27.8) * mm});
            skLineSegment(sketch, "E9.1.55.0", {"start": v(-31.62, -29.14) * mm, "end": v(-35.34, -32.49) * mm});
            skLineSegment(sketch, "E9.3.55.0", {"start": v(-32.29, -28.4) * mm, "end": v(-36, -31.75) * mm});
            skLineSegment(sketch, "E9.6.55.0", {"start": v(-31.96, -28.77) * mm, "end": v(-33.81, -30.45) * mm});
            skPoint(sketch, "E9.9.55.0", {"position": v(-33.81, -30.45) * mm});
            skLineSegment(sketch, "E9.10.55.0", {"start": v(-36, -31.75) * mm, "end": v(-35.34, -32.49) * mm});
            skLineSegment(sketch, "E9.13.55.0", {"start": v(-32.29, -28.4) * mm, "end": v(-31.62, -29.14) * mm});
            skLineSegment(sketch, "E9.1.56.0", {"start": v(-30.37, -30.44) * mm, "end": v(-33.94, -33.94) * mm});
            skLineSegment(sketch, "E9.3.56.0", {"start": v(-31.07, -29.73) * mm, "end": v(-34.64, -33.23) * mm});
            skLineSegment(sketch, "E9.6.56.0", {"start": v(-30.72, -30.09) * mm, "end": v(-32.5, -31.83) * mm});
            skPoint(sketch, "E9.9.56.0", {"position": v(-32.5, -31.83) * mm});
            skLineSegment(sketch, "E9.10.56.0", {"start": v(-34.64, -33.23) * mm, "end": v(-33.94, -33.94) * mm});
            skLineSegment(sketch, "E9.13.56.0", {"start": v(-31.07, -29.73) * mm, "end": v(-30.37, -30.44) * mm});
            skLineSegment(sketch, "E9.1.57.0", {"start": v(-29.07, -31.69) * mm, "end": v(-32.5, -35.33) * mm});
            skLineSegment(sketch, "E9.3.57.0", {"start": v(-29.8, -31) * mm, "end": v(-33.22, -34.65) * mm});
            skLineSegment(sketch, "E9.6.57.0", {"start": v(-29.44, -31.35) * mm, "end": v(-31.15, -33.17) * mm});
            skPoint(sketch, "E9.9.57.0", {"position": v(-31.15, -33.17) * mm});
            skLineSegment(sketch, "E9.10.57.0", {"start": v(-33.22, -34.65) * mm, "end": v(-32.5, -35.33) * mm});
            skLineSegment(sketch, "E9.13.57.0", {"start": v(-29.8, -31) * mm, "end": v(-29.07, -31.69) * mm});
            skLineSegment(sketch, "E9.1.58.0", {"start": v(-27.72, -32.88) * mm, "end": v(-30.99, -36.66) * mm});
            skLineSegment(sketch, "E9.3.58.0", {"start": v(-28.48, -32.22) * mm, "end": v(-31.74, -36) * mm});
            skLineSegment(sketch, "E9.6.58.0", {"start": v(-28.1, -32.55) * mm, "end": v(-29.73, -34.44) * mm});
            skPoint(sketch, "E9.9.58.0", {"position": v(-29.73, -34.44) * mm});
            skLineSegment(sketch, "E9.10.58.0", {"start": v(-31.74, -36) * mm, "end": v(-30.99, -36.66) * mm});
            skLineSegment(sketch, "E9.13.58.0", {"start": v(-28.48, -32.22) * mm, "end": v(-27.72, -32.88) * mm});
            skLineSegment(sketch, "E9.1.59.0", {"start": v(-26.32, -34) * mm, "end": v(-29.42, -37.93) * mm});
            skLineSegment(sketch, "E9.3.59.0", {"start": v(-27.1, -33.39) * mm, "end": v(-30.2, -37.3) * mm});
            skLineSegment(sketch, "E9.6.59.0", {"start": v(-26.7, -33.7) * mm, "end": v(-28.26, -35.66) * mm});
            skPoint(sketch, "E9.9.59.0", {"position": v(-28.26, -35.66) * mm});
            skLineSegment(sketch, "E9.10.59.0", {"start": v(-30.2, -37.3) * mm, "end": v(-29.42, -37.93) * mm});
            skLineSegment(sketch, "E9.13.59.0", {"start": v(-27.1, -33.39) * mm, "end": v(-26.32, -34) * mm});
            skLineSegment(sketch, "E9.1.60.0", {"start": v(-24.87, -35.08) * mm, "end": v(-27.8, -39.13) * mm});
            skLineSegment(sketch, "E9.3.60.0", {"start": v(-25.68, -34.5) * mm, "end": v(-28.62, -38.54) * mm});
            skLineSegment(sketch, "E9.6.60.0", {"start": v(-25.27, -34.79) * mm, "end": v(-26.74, -36.81) * mm});
            skPoint(sketch, "E9.9.60.0", {"position": v(-26.74, -36.81) * mm});
            skLineSegment(sketch, "E9.10.60.0", {"start": v(-28.62, -38.54) * mm, "end": v(-27.8, -39.13) * mm});
            skLineSegment(sketch, "E9.13.60.0", {"start": v(-25.68, -34.5) * mm, "end": v(-24.87, -35.08) * mm});
            skLineSegment(sketch, "E9.1.61.0", {"start": v(-23.38, -36.1) * mm, "end": v(-26.15, -40.26) * mm});
            skLineSegment(sketch, "E9.3.61.0", {"start": v(-24.21, -35.54) * mm, "end": v(-26.98, -39.7) * mm});
            skLineSegment(sketch, "E9.6.61.0", {"start": v(-23.8, -35.82) * mm, "end": v(-25.18, -37.9) * mm});
            skPoint(sketch, "E9.9.61.0", {"position": v(-25.18, -37.9) * mm});
            skLineSegment(sketch, "E9.10.61.0", {"start": v(-26.98, -39.7) * mm, "end": v(-26.15, -40.26) * mm});
            skLineSegment(sketch, "E9.13.61.0", {"start": v(-24.21, -35.54) * mm, "end": v(-23.38, -36.1) * mm});
            skLineSegment(sketch, "E9.1.62.0", {"start": v(-21.85, -37.04) * mm, "end": v(-24.44, -41.32) * mm});
            skLineSegment(sketch, "E9.3.62.0", {"start": v(-22.7, -36.52) * mm, "end": v(-25.3, -40.8) * mm});
            skLineSegment(sketch, "E9.6.62.0", {"start": v(-22.28, -36.78) * mm, "end": v(-23.57, -38.92) * mm});
            skPoint(sketch, "E9.9.62.0", {"position": v(-23.57, -38.92) * mm});
            skLineSegment(sketch, "E9.10.62.0", {"start": v(-25.3, -40.8) * mm, "end": v(-24.44, -41.32) * mm});
            skLineSegment(sketch, "E9.13.62.0", {"start": v(-22.7, -36.52) * mm, "end": v(-21.85, -37.04) * mm});
            skLineSegment(sketch, "E9.1.63.0", {"start": v(-20.28, -37.92) * mm, "end": v(-22.69, -42.3) * mm});
            skLineSegment(sketch, "E9.3.63.0", {"start": v(-21.15, -37.44) * mm, "end": v(-23.56, -41.82) * mm});
            skLineSegment(sketch, "E9.6.63.0", {"start": v(-20.72, -37.68) * mm, "end": v(-21.92, -39.87) * mm});
            skPoint(sketch, "E9.9.63.0", {"position": v(-21.92, -39.87) * mm});
            skLineSegment(sketch, "E9.10.63.0", {"start": v(-23.56, -41.82) * mm, "end": v(-22.69, -42.3) * mm});
            skLineSegment(sketch, "E9.13.63.0", {"start": v(-21.15, -37.44) * mm, "end": v(-20.28, -37.92) * mm});
            skLineSegment(sketch, "E9.1.64.0", {"start": v(-18.67, -38.74) * mm, "end": v(-20.9, -43.22) * mm});
            skLineSegment(sketch, "E9.3.64.0", {"start": v(-19.57, -38.3) * mm, "end": v(-21.8, -42.77) * mm});
            skLineSegment(sketch, "E9.6.64.0", {"start": v(-19.12, -38.52) * mm, "end": v(-20.23, -40.75) * mm});
            skPoint(sketch, "E9.9.64.0", {"position": v(-20.23, -40.75) * mm});
            skLineSegment(sketch, "E9.10.64.0", {"start": v(-21.8, -42.77) * mm, "end": v(-20.9, -43.22) * mm});
            skLineSegment(sketch, "E9.13.64.0", {"start": v(-19.57, -38.3) * mm, "end": v(-18.67, -38.74) * mm});
            skLineSegment(sketch, "E9.1.65.0", {"start": v(-17.03, -39.49) * mm, "end": v(-19.07, -44.05) * mm});
            skLineSegment(sketch, "E9.3.65.0", {"start": v(-17.95, -39.08) * mm, "end": v(-19.98, -43.65) * mm});
            skLineSegment(sketch, "E9.6.65.0", {"start": v(-17.49, -39.28) * mm, "end": v(-18.5, -41.57) * mm});
            skPoint(sketch, "E9.9.65.0", {"position": v(-18.5, -41.57) * mm});
            skLineSegment(sketch, "E9.10.65.0", {"start": v(-19.98, -43.65) * mm, "end": v(-19.07, -44.05) * mm});
            skLineSegment(sketch, "E9.13.65.0", {"start": v(-17.95, -39.08) * mm, "end": v(-17.03, -39.49) * mm});
            skLineSegment(sketch, "E9.1.66.0", {"start": v(-15.36, -40.16) * mm, "end": v(-17.2, -44.81) * mm});
            skLineSegment(sketch, "E9.3.66.0", {"start": v(-16.3, -39.8) * mm, "end": v(-18.13, -44.45) * mm});
            skLineSegment(sketch, "E9.6.66.0", {"start": v(-15.83, -39.98) * mm, "end": v(-16.75, -42.3) * mm});
            skPoint(sketch, "E9.9.66.0", {"position": v(-16.75, -42.3) * mm});
            skLineSegment(sketch, "E9.10.66.0", {"start": v(-18.13, -44.45) * mm, "end": v(-17.2, -44.81) * mm});
            skLineSegment(sketch, "E9.13.66.0", {"start": v(-16.3, -39.8) * mm, "end": v(-15.36, -40.16) * mm});
            skLineSegment(sketch, "E9.1.67.0", {"start": v(-13.67, -40.77) * mm, "end": v(-15.31, -45.5) * mm});
            skLineSegment(sketch, "E9.3.67.0", {"start": v(-14.61, -40.44) * mm, "end": v(-16.26, -45.17) * mm});
            skLineSegment(sketch, "E9.6.67.0", {"start": v(-14.14, -40.6) * mm, "end": v(-14.96, -42.97) * mm});
            skPoint(sketch, "E9.9.67.0", {"position": v(-14.96, -42.97) * mm});
            skLineSegment(sketch, "E9.10.67.0", {"start": v(-16.26, -45.17) * mm, "end": v(-15.31, -45.5) * mm});
            skLineSegment(sketch, "E9.13.67.0", {"start": v(-14.61, -40.44) * mm, "end": v(-13.67, -40.77) * mm});
            skLineSegment(sketch, "E9.1.68.0", {"start": v(-11.95, -41.3) * mm, "end": v(-13.4, -46.1) * mm});
            skLineSegment(sketch, "E9.3.68.0", {"start": v(-12.9, -41.02) * mm, "end": v(-14.35, -45.8) * mm});
            skLineSegment(sketch, "E9.6.68.0", {"start": v(-12.43, -41.16) * mm, "end": v(-13.15, -43.56) * mm});
            skPoint(sketch, "E9.9.68.0", {"position": v(-13.15, -43.56) * mm});
            skLineSegment(sketch, "E9.10.68.0", {"start": v(-14.35, -45.8) * mm, "end": v(-13.4, -46.1) * mm});
            skLineSegment(sketch, "E9.13.68.0", {"start": v(-12.9, -41.02) * mm, "end": v(-11.95, -41.3) * mm});
            skLineSegment(sketch, "E9.1.69.0", {"start": v(-10.2, -41.77) * mm, "end": v(-11.45, -46.62) * mm});
            skLineSegment(sketch, "E9.3.69.0", {"start": v(-11.18, -41.52) * mm, "end": v(-12.42, -46.37) * mm});
            skLineSegment(sketch, "E9.6.69.0", {"start": v(-10.7, -41.65) * mm, "end": v(-11.32, -44.07) * mm});
            skPoint(sketch, "E9.9.69.0", {"position": v(-11.32, -44.07) * mm});
            skLineSegment(sketch, "E9.10.69.0", {"start": v(-12.42, -46.37) * mm, "end": v(-11.45, -46.62) * mm});
            skLineSegment(sketch, "E9.13.69.0", {"start": v(-11.18, -41.52) * mm, "end": v(-10.2, -41.77) * mm});
            skLineSegment(sketch, "E10.1.70.0", {"start": v(-8.45, -42.16) * mm, "end": v(-9.5, -47.06) * mm});
            skLineSegment(sketch, "E10.3.70.0", {"start": v(-9.43, -41.96) * mm, "end": v(-10.47, -46.85) * mm});
            skLineSegment(sketch, "E10.6.70.0", {"start": v(-8.94, -42.06) * mm, "end": v(-9.46, -44.5) * mm});
            skPoint(sketch, "E10.9.70.0", {"position": v(-9.46, -44.5) * mm});
            skLineSegment(sketch, "E10.10.70.0", {"start": v(-10.47, -46.85) * mm, "end": v(-9.5, -47.06) * mm});
            skLineSegment(sketch, "E10.13.70.0", {"start": v(-9.43, -41.96) * mm, "end": v(-8.45, -42.16) * mm});
            skLineSegment(sketch, "E10.1.71.0", {"start": v(-6.68, -42.48) * mm, "end": v(-7.51, -47.41) * mm});
            skLineSegment(sketch, "E10.3.71.0", {"start": v(-7.66, -42.31) * mm, "end": v(-8.5, -47.24) * mm});
            skLineSegment(sketch, "E10.6.71.0", {"start": v(-7.17, -42.4) * mm, "end": v(-7.59, -44.86) * mm});
            skPoint(sketch, "E10.9.71.0", {"position": v(-7.59, -44.86) * mm});
            skLineSegment(sketch, "E10.10.71.0", {"start": v(-8.5, -47.24) * mm, "end": v(-7.51, -47.41) * mm});
            skLineSegment(sketch, "E10.13.71.0", {"start": v(-7.66, -42.31) * mm, "end": v(-6.68, -42.48) * mm});
            skLineSegment(sketch, "E10.1.72.0", {"start": v(-4.9, -42.72) * mm, "end": v(-5.52, -47.68) * mm});
            skLineSegment(sketch, "E10.3.72.0", {"start": v(-5.89, -42.6) * mm, "end": v(-6.51, -47.56) * mm});
            skLineSegment(sketch, "E10.6.72.0", {"start": v(-5.39, -42.66) * mm, "end": v(-5.7, -45.14) * mm});
            skPoint(sketch, "E10.9.72.0", {"position": v(-5.7, -45.14) * mm});
            skLineSegment(sketch, "E10.10.72.0", {"start": v(-6.51, -47.56) * mm, "end": v(-5.52, -47.68) * mm});
            skLineSegment(sketch, "E10.13.72.0", {"start": v(-5.89, -42.6) * mm, "end": v(-4.9, -42.72) * mm});
            skLineSegment(sketch, "E10.1.73.0", {"start": v(-3.1, -42.9) * mm, "end": v(-3.52, -47.87) * mm});
            skLineSegment(sketch, "E10.3.73.0", {"start": v(-4.1, -42.8) * mm, "end": v(-4.51, -47.79) * mm});
            skLineSegment(sketch, "E10.6.73.0", {"start": v(-3.6, -42.85) * mm, "end": v(-3.8, -45.34) * mm});
            skPoint(sketch, "E10.9.73.0", {"position": v(-3.8, -45.34) * mm});
            skLineSegment(sketch, "E10.10.73.0", {"start": v(-4.51, -47.79) * mm, "end": v(-3.52, -47.87) * mm});
            skLineSegment(sketch, "E10.13.73.0", {"start": v(-4.1, -42.8) * mm, "end": v(-3.1, -42.9) * mm});
            skLineSegment(sketch, "E10.1.74.0", {"start": v(-1.3, -42.98) * mm, "end": v(-1.51, -47.98) * mm});
            skLineSegment(sketch, "E10.3.74.0", {"start": v(-2.3, -42.94) * mm, "end": v(-2.5, -47.94) * mm});
            skLineSegment(sketch, "E10.6.74.0", {"start": v(-1.8, -42.96) * mm, "end": v(-1.9, -45.46) * mm});
            skPoint(sketch, "E10.9.74.0", {"position": v(-1.9, -45.46) * mm});
            skLineSegment(sketch, "E10.10.74.0", {"start": v(-2.5, -47.94) * mm, "end": v(-1.51, -47.98) * mm});
            skLineSegment(sketch, "E10.13.74.0", {"start": v(-2.3, -42.94) * mm, "end": v(-1.3, -42.98) * mm});
            skLineSegment(sketch, "E10.1.75.0", {"start": v(0.5, -43) * mm, "end": v(0.5, -48) * mm});
            skLineSegment(sketch, "E10.3.75.0", {"start": v(-0.5, -43) * mm, "end": v(-0.5, -48) * mm});
            skLineSegment(sketch, "E10.6.75.0", {"start": v(0, -43) * mm, "end": v(0, -45.5) * mm});
            skPoint(sketch, "E10.9.75.0", {"position": v(0, -45.5) * mm});
            skLineSegment(sketch, "E10.10.75.0", {"start": v(-0.5, -48) * mm, "end": v(0.5, -48) * mm});
            skLineSegment(sketch, "E10.13.75.0", {"start": v(-0.5, -43) * mm, "end": v(0.5, -43) * mm});
            skLineSegment(sketch, "E10.1.76.0", {"start": v(2.3, -42.94) * mm, "end": v(2.5, -47.94) * mm});
            skLineSegment(sketch, "E10.3.76.0", {"start": v(1.3, -42.98) * mm, "end": v(1.51, -47.98) * mm});
            skLineSegment(sketch, "E10.6.76.0", {"start": v(1.8, -42.96) * mm, "end": v(1.9, -45.46) * mm});
            skPoint(sketch, "E10.9.76.0", {"position": v(1.9, -45.46) * mm});
            skLineSegment(sketch, "E10.10.76.0", {"start": v(1.51, -47.98) * mm, "end": v(2.5, -47.94) * mm});
            skLineSegment(sketch, "E10.13.76.0", {"start": v(1.3, -42.98) * mm, "end": v(2.3, -42.94) * mm});
            skLineSegment(sketch, "E10.1.77.0", {"start": v(4.1, -42.8) * mm, "end": v(4.51, -47.79) * mm});
            skLineSegment(sketch, "E10.3.77.0", {"start": v(3.1, -42.9) * mm, "end": v(3.52, -47.87) * mm});
            skLineSegment(sketch, "E10.6.77.0", {"start": v(3.6, -42.85) * mm, "end": v(3.8, -45.34) * mm});
            skPoint(sketch, "E10.9.77.0", {"position": v(3.8, -45.34) * mm});
            skLineSegment(sketch, "E10.10.77.0", {"start": v(3.52, -47.87) * mm, "end": v(4.51, -47.79) * mm});
            skLineSegment(sketch, "E10.13.77.0", {"start": v(3.1, -42.9) * mm, "end": v(4.1, -42.8) * mm});
            skLineSegment(sketch, "E10.1.78.0", {"start": v(5.89, -42.6) * mm, "end": v(6.51, -47.56) * mm});
            skLineSegment(sketch, "E10.3.78.0", {"start": v(4.9, -42.72) * mm, "end": v(5.52, -47.68) * mm});
            skLineSegment(sketch, "E10.6.78.0", {"start": v(5.39, -42.66) * mm, "end": v(5.7, -45.14) * mm});
            skPoint(sketch, "E10.9.78.0", {"position": v(5.7, -45.14) * mm});
            skLineSegment(sketch, "E10.10.78.0", {"start": v(5.52, -47.68) * mm, "end": v(6.51, -47.56) * mm});
            skLineSegment(sketch, "E10.13.78.0", {"start": v(4.9, -42.72) * mm, "end": v(5.89, -42.6) * mm});
            skLineSegment(sketch, "E10.1.79.0", {"start": v(7.66, -42.31) * mm, "end": v(8.5, -47.24) * mm});
            skLineSegment(sketch, "E10.3.79.0", {"start": v(6.68, -42.48) * mm, "end": v(7.51, -47.41) * mm});
            skLineSegment(sketch, "E10.6.79.0", {"start": v(7.17, -42.4) * mm, "end": v(7.59, -44.86) * mm});
            skPoint(sketch, "E10.9.79.0", {"position": v(7.59, -44.86) * mm});
            skLineSegment(sketch, "E10.10.79.0", {"start": v(7.51, -47.41) * mm, "end": v(8.5, -47.24) * mm});
            skLineSegment(sketch, "E10.13.79.0", {"start": v(6.68, -42.48) * mm, "end": v(7.66, -42.31) * mm});
            skLineSegment(sketch, "E10.1.80.0", {"start": v(9.43, -41.96) * mm, "end": v(10.47, -46.85) * mm});
            skLineSegment(sketch, "E10.3.80.0", {"start": v(8.45, -42.16) * mm, "end": v(9.5, -47.06) * mm});
            skLineSegment(sketch, "E10.6.80.0", {"start": v(8.94, -42.06) * mm, "end": v(9.46, -44.5) * mm});
            skPoint(sketch, "E10.9.80.0", {"position": v(9.46, -44.5) * mm});
            skLineSegment(sketch, "E10.10.80.0", {"start": v(9.5, -47.06) * mm, "end": v(10.47, -46.85) * mm});
            skLineSegment(sketch, "E10.13.80.0", {"start": v(8.45, -42.16) * mm, "end": v(9.43, -41.96) * mm});
            skLineSegment(sketch, "E10.1.81.0", {"start": v(11.18, -41.52) * mm, "end": v(12.42, -46.37) * mm});
            skLineSegment(sketch, "E10.3.81.0", {"start": v(10.2, -41.77) * mm, "end": v(11.45, -46.62) * mm});
            skLineSegment(sketch, "E10.6.81.0", {"start": v(10.7, -41.65) * mm, "end": v(11.32, -44.07) * mm});
            skPoint(sketch, "E10.9.81.0", {"position": v(11.32, -44.07) * mm});
            skLineSegment(sketch, "E10.10.81.0", {"start": v(11.45, -46.62) * mm, "end": v(12.42, -46.37) * mm});
            skLineSegment(sketch, "E10.13.81.0", {"start": v(10.2, -41.77) * mm, "end": v(11.18, -41.52) * mm});
            skLineSegment(sketch, "E10.1.82.0", {"start": v(12.9, -41.02) * mm, "end": v(14.35, -45.8) * mm});
            skLineSegment(sketch, "E10.3.82.0", {"start": v(11.95, -41.3) * mm, "end": v(13.4, -46.1) * mm});
            skLineSegment(sketch, "E10.6.82.0", {"start": v(12.43, -41.16) * mm, "end": v(13.15, -43.56) * mm});
            skPoint(sketch, "E10.9.82.0", {"position": v(13.15, -43.56) * mm});
            skLineSegment(sketch, "E10.10.82.0", {"start": v(13.4, -46.1) * mm, "end": v(14.35, -45.8) * mm});
            skLineSegment(sketch, "E10.13.82.0", {"start": v(11.95, -41.3) * mm, "end": v(12.9, -41.02) * mm});
            skLineSegment(sketch, "E10.1.83.0", {"start": v(14.61, -40.44) * mm, "end": v(16.26, -45.17) * mm});
            skLineSegment(sketch, "E10.3.83.0", {"start": v(13.67, -40.77) * mm, "end": v(15.31, -45.5) * mm});
            skLineSegment(sketch, "E10.6.83.0", {"start": v(14.14, -40.6) * mm, "end": v(14.96, -42.97) * mm});
            skPoint(sketch, "E10.9.83.0", {"position": v(14.96, -42.97) * mm});
            skLineSegment(sketch, "E10.10.83.0", {"start": v(15.31, -45.5) * mm, "end": v(16.26, -45.17) * mm});
            skLineSegment(sketch, "E10.13.83.0", {"start": v(13.67, -40.77) * mm, "end": v(14.61, -40.44) * mm});
            skLineSegment(sketch, "E10.1.84.0", {"start": v(16.3, -39.8) * mm, "end": v(18.13, -44.45) * mm});
            skLineSegment(sketch, "E10.3.84.0", {"start": v(15.36, -40.16) * mm, "end": v(17.2, -44.81) * mm});
            skLineSegment(sketch, "E10.6.84.0", {"start": v(15.83, -39.98) * mm, "end": v(16.75, -42.3) * mm});
            skPoint(sketch, "E10.9.84.0", {"position": v(16.75, -42.3) * mm});
            skLineSegment(sketch, "E10.10.84.0", {"start": v(17.2, -44.81) * mm, "end": v(18.13, -44.45) * mm});
            skLineSegment(sketch, "E10.13.84.0", {"start": v(15.36, -40.16) * mm, "end": v(16.3, -39.8) * mm});
            skLineSegment(sketch, "E10.1.85.0", {"start": v(17.95, -39.08) * mm, "end": v(19.98, -43.65) * mm});
            skLineSegment(sketch, "E10.3.85.0", {"start": v(17.03, -39.49) * mm, "end": v(19.07, -44.05) * mm});
            skLineSegment(sketch, "E10.6.85.0", {"start": v(17.49, -39.28) * mm, "end": v(18.5, -41.57) * mm});
            skPoint(sketch, "E10.9.85.0", {"position": v(18.5, -41.57) * mm});
            skLineSegment(sketch, "E10.10.85.0", {"start": v(19.07, -44.05) * mm, "end": v(19.98, -43.65) * mm});
            skLineSegment(sketch, "E10.13.85.0", {"start": v(17.03, -39.49) * mm, "end": v(17.95, -39.08) * mm});
            skLineSegment(sketch, "E10.1.86.0", {"start": v(19.57, -38.3) * mm, "end": v(21.8, -42.77) * mm});
            skLineSegment(sketch, "E10.3.86.0", {"start": v(18.67, -38.74) * mm, "end": v(20.9, -43.22) * mm});
            skLineSegment(sketch, "E10.6.86.0", {"start": v(19.12, -38.52) * mm, "end": v(20.23, -40.75) * mm});
            skPoint(sketch, "E10.9.86.0", {"position": v(20.23, -40.75) * mm});
            skLineSegment(sketch, "E10.10.86.0", {"start": v(20.9, -43.22) * mm, "end": v(21.8, -42.77) * mm});
            skLineSegment(sketch, "E10.13.86.0", {"start": v(18.67, -38.74) * mm, "end": v(19.57, -38.3) * mm});
            skLineSegment(sketch, "E10.1.87.0", {"start": v(21.15, -37.44) * mm, "end": v(23.56, -41.82) * mm});
            skLineSegment(sketch, "E10.3.87.0", {"start": v(20.28, -37.92) * mm, "end": v(22.69, -42.3) * mm});
            skLineSegment(sketch, "E10.6.87.0", {"start": v(20.72, -37.68) * mm, "end": v(21.92, -39.87) * mm});
            skPoint(sketch, "E10.9.87.0", {"position": v(21.92, -39.87) * mm});
            skLineSegment(sketch, "E10.10.87.0", {"start": v(22.69, -42.3) * mm, "end": v(23.56, -41.82) * mm});
            skLineSegment(sketch, "E10.13.87.0", {"start": v(20.28, -37.92) * mm, "end": v(21.15, -37.44) * mm});
            skLineSegment(sketch, "E10.1.88.0", {"start": v(22.7, -36.52) * mm, "end": v(25.3, -40.8) * mm});
            skLineSegment(sketch, "E10.3.88.0", {"start": v(21.85, -37.04) * mm, "end": v(24.44, -41.32) * mm});
            skLineSegment(sketch, "E10.6.88.0", {"start": v(22.28, -36.78) * mm, "end": v(23.57, -38.92) * mm});
            skPoint(sketch, "E10.9.88.0", {"position": v(23.57, -38.92) * mm});
            skLineSegment(sketch, "E10.10.88.0", {"start": v(24.44, -41.32) * mm, "end": v(25.3, -40.8) * mm});
            skLineSegment(sketch, "E10.13.88.0", {"start": v(21.85, -37.04) * mm, "end": v(22.7, -36.52) * mm});
            skLineSegment(sketch, "E10.1.89.0", {"start": v(24.21, -35.54) * mm, "end": v(26.98, -39.7) * mm});
            skLineSegment(sketch, "E10.3.89.0", {"start": v(23.38, -36.1) * mm, "end": v(26.15, -40.26) * mm});
            skLineSegment(sketch, "E10.6.89.0", {"start": v(23.8, -35.82) * mm, "end": v(25.18, -37.9) * mm});
            skPoint(sketch, "E10.9.89.0", {"position": v(25.18, -37.9) * mm});
            skLineSegment(sketch, "E10.10.89.0", {"start": v(26.15, -40.26) * mm, "end": v(26.98, -39.7) * mm});
            skLineSegment(sketch, "E10.13.89.0", {"start": v(23.38, -36.1) * mm, "end": v(24.21, -35.54) * mm});
            skLineSegment(sketch, "E10.1.90.0", {"start": v(25.68, -34.5) * mm, "end": v(28.62, -38.54) * mm});
            skLineSegment(sketch, "E10.3.90.0", {"start": v(24.87, -35.08) * mm, "end": v(27.8, -39.13) * mm});
            skLineSegment(sketch, "E10.6.90.0", {"start": v(25.27, -34.79) * mm, "end": v(26.74, -36.81) * mm});
            skPoint(sketch, "E10.9.90.0", {"position": v(26.74, -36.81) * mm});
            skLineSegment(sketch, "E10.10.90.0", {"start": v(27.8, -39.13) * mm, "end": v(28.62, -38.54) * mm});
            skLineSegment(sketch, "E10.13.90.0", {"start": v(24.87, -35.08) * mm, "end": v(25.68, -34.5) * mm});
            skLineSegment(sketch, "E10.1.91.0", {"start": v(27.1, -33.39) * mm, "end": v(30.2, -37.3) * mm});
            skLineSegment(sketch, "E10.3.91.0", {"start": v(26.32, -34) * mm, "end": v(29.42, -37.93) * mm});
            skLineSegment(sketch, "E10.6.91.0", {"start": v(26.7, -33.7) * mm, "end": v(28.26, -35.66) * mm});
            skPoint(sketch, "E10.9.91.0", {"position": v(28.26, -35.66) * mm});
            skLineSegment(sketch, "E10.10.91.0", {"start": v(29.42, -37.93) * mm, "end": v(30.2, -37.3) * mm});
            skLineSegment(sketch, "E10.13.91.0", {"start": v(26.32, -34) * mm, "end": v(27.1, -33.39) * mm});
            skLineSegment(sketch, "E10.1.92.0", {"start": v(28.48, -32.22) * mm, "end": v(31.74, -36) * mm});
            skLineSegment(sketch, "E10.3.92.0", {"start": v(27.72, -32.88) * mm, "end": v(30.99, -36.66) * mm});
            skLineSegment(sketch, "E10.6.92.0", {"start": v(28.1, -32.55) * mm, "end": v(29.73, -34.44) * mm});
            skPoint(sketch, "E10.9.92.0", {"position": v(29.73, -34.44) * mm});
            skLineSegment(sketch, "E10.10.92.0", {"start": v(30.99, -36.66) * mm, "end": v(31.74, -36) * mm});
            skLineSegment(sketch, "E10.13.92.0", {"start": v(27.72, -32.88) * mm, "end": v(28.48, -32.22) * mm});
            skLineSegment(sketch, "E10.1.93.0", {"start": v(29.8, -31) * mm, "end": v(33.22, -34.65) * mm});
            skLineSegment(sketch, "E10.3.93.0", {"start": v(29.07, -31.69) * mm, "end": v(32.5, -35.33) * mm});
            skLineSegment(sketch, "E10.6.93.0", {"start": v(29.44, -31.35) * mm, "end": v(31.15, -33.17) * mm});
            skPoint(sketch, "E10.9.93.0", {"position": v(31.15, -33.17) * mm});
            skLineSegment(sketch, "E10.10.93.0", {"start": v(32.5, -35.33) * mm, "end": v(33.22, -34.65) * mm});
            skLineSegment(sketch, "E10.13.93.0", {"start": v(29.07, -31.69) * mm, "end": v(29.8, -31) * mm});
            skLineSegment(sketch, "E10.1.94.0", {"start": v(31.07, -29.73) * mm, "end": v(34.64, -33.23) * mm});
            skLineSegment(sketch, "E10.3.94.0", {"start": v(30.37, -30.44) * mm, "end": v(33.94, -33.94) * mm});
            skLineSegment(sketch, "E10.6.94.0", {"start": v(30.72, -30.09) * mm, "end": v(32.5, -31.83) * mm});
            skPoint(sketch, "E10.9.94.0", {"position": v(32.5, -31.83) * mm});
            skLineSegment(sketch, "E10.10.94.0", {"start": v(33.94, -33.94) * mm, "end": v(34.64, -33.23) * mm});
            skLineSegment(sketch, "E10.13.94.0", {"start": v(30.37, -30.44) * mm, "end": v(31.07, -29.73) * mm});
            skLineSegment(sketch, "E10.1.95.0", {"start": v(32.29, -28.4) * mm, "end": v(36, -31.75) * mm});
            skLineSegment(sketch, "E10.3.95.0", {"start": v(31.62, -29.14) * mm, "end": v(35.34, -32.49) * mm});
            skLineSegment(sketch, "E10.6.95.0", {"start": v(31.96, -28.77) * mm, "end": v(33.81, -30.45) * mm});
            skPoint(sketch, "E10.9.95.0", {"position": v(33.81, -30.45) * mm});
            skLineSegment(sketch, "E10.10.95.0", {"start": v(35.34, -32.49) * mm, "end": v(36, -31.75) * mm});
            skLineSegment(sketch, "E10.13.95.0", {"start": v(31.62, -29.14) * mm, "end": v(32.29, -28.4) * mm});
            skLineSegment(sketch, "E10.1.96.0", {"start": v(33.45, -27.02) * mm, "end": v(37.3, -30.21) * mm});
            skLineSegment(sketch, "E10.3.96.0", {"start": v(32.81, -27.8) * mm, "end": v(36.67, -30.98) * mm});
            skLineSegment(sketch, "E10.6.96.0", {"start": v(33.13, -27.4) * mm, "end": v(35.06, -29) * mm});
            skPoint(sketch, "E10.9.96.0", {"position": v(35.06, -29) * mm});
            skLineSegment(sketch, "E10.10.96.0", {"start": v(36.67, -30.98) * mm, "end": v(37.3, -30.21) * mm});
            skLineSegment(sketch, "E10.13.96.0", {"start": v(32.81, -27.8) * mm, "end": v(33.45, -27.02) * mm});
            skLineSegment(sketch, "E10.1.97.0", {"start": v(34.55, -25.6) * mm, "end": v(38.54, -28.62) * mm});
            skLineSegment(sketch, "E10.3.97.0", {"start": v(33.95, -26.4) * mm, "end": v(37.93, -29.42) * mm});
            skLineSegment(sketch, "E10.6.97.0", {"start": v(34.25, -26) * mm, "end": v(36.24, -27.5) * mm});
            skPoint(sketch, "E10.9.97.0", {"position": v(36.24, -27.5) * mm});
            skLineSegment(sketch, "E10.10.97.0", {"start": v(37.93, -29.42) * mm, "end": v(38.54, -28.62) * mm});
            skLineSegment(sketch, "E10.13.97.0", {"start": v(33.95, -26.4) * mm, "end": v(34.55, -25.6) * mm});
            skLineSegment(sketch, "E10.1.98.0", {"start": v(35.6, -24.13) * mm, "end": v(39.7, -26.98) * mm});
            skLineSegment(sketch, "E10.3.98.0", {"start": v(35.02, -24.95) * mm, "end": v(39.13, -27.8) * mm});
            skLineSegment(sketch, "E10.6.98.0", {"start": v(35.3, -24.54) * mm, "end": v(37.36, -25.97) * mm});
            skPoint(sketch, "E10.9.98.0", {"position": v(37.36, -25.97) * mm});
            skLineSegment(sketch, "E10.10.98.0", {"start": v(39.13, -27.8) * mm, "end": v(39.7, -26.98) * mm});
            skLineSegment(sketch, "E10.13.98.0", {"start": v(35.02, -24.95) * mm, "end": v(35.6, -24.13) * mm});
            skLineSegment(sketch, "E10.1.99.0", {"start": v(36.57, -22.62) * mm, "end": v(40.8, -25.3) * mm});
            skLineSegment(sketch, "E10.3.99.0", {"start": v(36.04, -23.46) * mm, "end": v(40.26, -26.14) * mm});
            skLineSegment(sketch, "E10.6.99.0", {"start": v(36.3, -23.04) * mm, "end": v(38.42, -24.38) * mm});
            skPoint(sketch, "E10.9.99.0", {"position": v(38.42, -24.38) * mm});
            skLineSegment(sketch, "E10.10.99.0", {"start": v(40.26, -26.14) * mm, "end": v(40.8, -25.3) * mm});
            skLineSegment(sketch, "E10.13.99.0", {"start": v(36.04, -23.46) * mm, "end": v(36.57, -22.62) * mm});
            skLineSegment(sketch, "E11.1.100.0", {"start": v(37.49, -21.07) * mm, "end": v(41.82, -23.57) * mm});
            skLineSegment(sketch, "E11.3.100.0", {"start": v(36.99, -21.93) * mm, "end": v(41.32, -24.43) * mm});
            skLineSegment(sketch, "E11.6.100.0", {"start": v(37.24, -21.5) * mm, "end": v(39.4, -22.75) * mm});
            skPoint(sketch, "E11.9.100.0", {"position": v(39.4, -22.75) * mm});
            skLineSegment(sketch, "E11.10.100.0", {"start": v(41.32, -24.43) * mm, "end": v(41.82, -23.57) * mm});
            skLineSegment(sketch, "E11.13.100.0", {"start": v(36.99, -21.93) * mm, "end": v(37.49, -21.07) * mm});
            skLineSegment(sketch, "E11.1.101.0", {"start": v(38.34, -19.48) * mm, "end": v(42.77, -21.8) * mm});
            skLineSegment(sketch, "E11.3.101.0", {"start": v(37.88, -20.36) * mm, "end": v(42.3, -22.68) * mm});
            skLineSegment(sketch, "E11.6.101.0", {"start": v(38.1, -19.92) * mm, "end": v(40.32, -21.08) * mm});
            skPoint(sketch, "E11.9.101.0", {"position": v(40.32, -21.08) * mm});
            skLineSegment(sketch, "E11.10.101.0", {"start": v(42.3, -22.68) * mm, "end": v(42.77, -21.8) * mm});
            skLineSegment(sketch, "E11.13.101.0", {"start": v(37.88, -20.36) * mm, "end": v(38.34, -19.48) * mm});
            skLineSegment(sketch, "E11.1.102.0", {"start": v(39.12, -17.86) * mm, "end": v(43.64, -19.98) * mm});
            skLineSegment(sketch, "E11.3.102.0", {"start": v(38.7, -18.76) * mm, "end": v(43.22, -20.89) * mm});
            skLineSegment(sketch, "E11.6.102.0", {"start": v(38.9, -18.3) * mm, "end": v(41.17, -19.37) * mm});
            skPoint(sketch, "E11.9.102.0", {"position": v(41.17, -19.37) * mm});
            skLineSegment(sketch, "E11.10.102.0", {"start": v(43.22, -20.89) * mm, "end": v(43.64, -19.98) * mm});
            skLineSegment(sketch, "E11.13.102.0", {"start": v(38.7, -18.76) * mm, "end": v(39.12, -17.86) * mm});
            skLineSegment(sketch, "E11.1.103.0", {"start": v(39.83, -16.2) * mm, "end": v(44.44, -18.14) * mm});
            skLineSegment(sketch, "E11.3.103.0", {"start": v(39.45, -17.12) * mm, "end": v(44.06, -19.06) * mm});
            skLineSegment(sketch, "E11.6.103.0", {"start": v(39.64, -16.66) * mm, "end": v(41.94, -17.63) * mm});
            skPoint(sketch, "E11.9.103.0", {"position": v(41.94, -17.63) * mm});
            skLineSegment(sketch, "E11.10.103.0", {"start": v(44.06, -19.06) * mm, "end": v(44.44, -18.14) * mm});
            skLineSegment(sketch, "E11.13.103.0", {"start": v(39.45, -17.12) * mm, "end": v(39.83, -16.2) * mm});
            skLineSegment(sketch, "E11.1.104.0", {"start": v(40.48, -14.52) * mm, "end": v(45.16, -16.26) * mm});
            skLineSegment(sketch, "E11.3.104.0", {"start": v(40.13, -15.46) * mm, "end": v(44.82, -17.2) * mm});
            skLineSegment(sketch, "E11.6.104.0", {"start": v(40.3, -14.99) * mm, "end": v(42.65, -15.86) * mm});
            skPoint(sketch, "E11.9.104.0", {"position": v(42.65, -15.86) * mm});
            skLineSegment(sketch, "E11.10.104.0", {"start": v(44.82, -17.2) * mm, "end": v(45.16, -16.26) * mm});
            skLineSegment(sketch, "E11.13.104.0", {"start": v(40.13, -15.46) * mm, "end": v(40.48, -14.52) * mm});
            skLineSegment(sketch, "E11.1.105.0", {"start": v(41.05, -12.81) * mm, "end": v(45.8, -14.36) * mm});
            skLineSegment(sketch, "E11.3.105.0", {"start": v(40.74, -13.76) * mm, "end": v(45.5, -15.3) * mm});
            skLineSegment(sketch, "E11.6.105.0", {"start": v(40.9, -13.29) * mm, "end": v(43.27, -14.06) * mm});
            skPoint(sketch, "E11.9.105.0", {"position": v(43.27, -14.06) * mm});
            skLineSegment(sketch, "E11.10.105.0", {"start": v(45.5, -15.3) * mm, "end": v(45.8, -14.36) * mm});
            skLineSegment(sketch, "E11.13.105.0", {"start": v(40.74, -13.76) * mm, "end": v(41.05, -12.81) * mm});
            skLineSegment(sketch, "E11.1.106.0", {"start": v(41.55, -11.08) * mm, "end": v(46.37, -12.43) * mm});
            skLineSegment(sketch, "E11.3.106.0", {"start": v(41.28, -12.05) * mm, "end": v(46.1, -13.39) * mm});
            skLineSegment(sketch, "E11.6.106.0", {"start": v(41.42, -11.56) * mm, "end": v(43.82, -12.24) * mm});
            skPoint(sketch, "E11.9.106.0", {"position": v(43.82, -12.24) * mm});
            skLineSegment(sketch, "E11.10.106.0", {"start": v(46.1, -13.39) * mm, "end": v(46.37, -12.43) * mm});
            skLineSegment(sketch, "E11.13.106.0", {"start": v(41.28, -12.05) * mm, "end": v(41.55, -11.08) * mm});
            skLineSegment(sketch, "E11.1.107.0", {"start": v(41.98, -9.33) * mm, "end": v(46.85, -10.47) * mm});
            skLineSegment(sketch, "E11.3.107.0", {"start": v(41.75, -10.3) * mm, "end": v(46.62, -11.45) * mm});
            skLineSegment(sketch, "E11.6.107.0", {"start": v(41.86, -9.82) * mm, "end": v(44.3, -10.39) * mm});
            skPoint(sketch, "E11.9.107.0", {"position": v(44.3, -10.39) * mm});
            skLineSegment(sketch, "E11.10.107.0", {"start": v(46.62, -11.45) * mm, "end": v(46.85, -10.47) * mm});
            skLineSegment(sketch, "E11.13.107.0", {"start": v(41.75, -10.3) * mm, "end": v(41.98, -9.33) * mm});
            skLineSegment(sketch, "E11.1.108.0", {"start": v(42.33, -7.57) * mm, "end": v(47.24, -8.5) * mm});
            skLineSegment(sketch, "E11.3.108.0", {"start": v(42.14, -8.55) * mm, "end": v(47.06, -9.49) * mm});
            skLineSegment(sketch, "E11.6.108.0", {"start": v(42.24, -8.06) * mm, "end": v(44.7, -8.53) * mm});
            skPoint(sketch, "E11.9.108.0", {"position": v(44.7, -8.53) * mm});
            skLineSegment(sketch, "E11.10.108.0", {"start": v(47.06, -9.49) * mm, "end": v(47.24, -8.5) * mm});
            skLineSegment(sketch, "E11.13.108.0", {"start": v(42.14, -8.55) * mm, "end": v(42.33, -7.57) * mm});
            skLineSegment(sketch, "E11.1.109.0", {"start": v(42.61, -5.79) * mm, "end": v(47.56, -6.52) * mm});
            skLineSegment(sketch, "E11.3.109.0", {"start": v(42.47, -6.78) * mm, "end": v(47.41, -7.5) * mm});
            skLineSegment(sketch, "E11.6.109.0", {"start": v(42.54, -6.28) * mm, "end": v(45.01, -6.65) * mm});
            skPoint(sketch, "E11.9.109.0", {"position": v(45.01, -6.65) * mm});
            skLineSegment(sketch, "E11.10.109.0", {"start": v(47.41, -7.5) * mm, "end": v(47.56, -6.52) * mm});
            skLineSegment(sketch, "E11.13.109.0", {"start": v(42.47, -6.78) * mm, "end": v(42.61, -5.79) * mm});
            skLineSegment(sketch, "E11.1.110.0", {"start": v(42.82, -4) * mm, "end": v(47.79, -4.52) * mm});
            skLineSegment(sketch, "E11.3.110.0", {"start": v(42.71, -5) * mm, "end": v(47.68, -5.51) * mm});
            skLineSegment(sketch, "E11.6.110.0", {"start": v(42.76, -4.5) * mm, "end": v(45.25, -4.76) * mm});
            skPoint(sketch, "E11.9.110.0", {"position": v(45.25, -4.76) * mm});
            skLineSegment(sketch, "E11.10.110.0", {"start": v(47.68, -5.51) * mm, "end": v(47.79, -4.52) * mm});
            skLineSegment(sketch, "E11.13.110.0", {"start": v(42.71, -5) * mm, "end": v(42.82, -4) * mm});
            skLineSegment(sketch, "E11.1.111.0", {"start": v(42.95, -2.2) * mm, "end": v(47.94, -2.51) * mm});
            skLineSegment(sketch, "E11.3.111.0", {"start": v(42.88, -3.2) * mm, "end": v(47.87, -3.51) * mm});
            skLineSegment(sketch, "E11.6.111.0", {"start": v(42.92, -2.7) * mm, "end": v(45.41, -2.86) * mm});
            skPoint(sketch, "E11.9.111.0", {"position": v(45.41, -2.86) * mm});
            skLineSegment(sketch, "E11.10.111.0", {"start": v(47.87, -3.51) * mm, "end": v(47.94, -2.51) * mm});
            skLineSegment(sketch, "E11.13.111.0", {"start": v(42.88, -3.2) * mm, "end": v(42.95, -2.2) * mm});
            skLineSegment(sketch, "E11.1.112.0", {"start": v(43, -0.4) * mm, "end": v(48, -0.5) * mm});
            skLineSegment(sketch, "E11.3.112.0", {"start": v(42.98, -1.4) * mm, "end": v(47.98, -1.5) * mm});
            skLineSegment(sketch, "E11.6.112.0", {"start": v(43, -0.9) * mm, "end": v(45.5, -0.95) * mm});
            skPoint(sketch, "E11.9.112.0", {"position": v(45.5, -0.95) * mm});
            skLineSegment(sketch, "E11.10.112.0", {"start": v(47.98, -1.5) * mm, "end": v(48, -0.5) * mm});
            skLineSegment(sketch, "E11.13.112.0", {"start": v(42.98, -1.4) * mm, "end": v(43, -0.4) * mm});
            skLineSegment(sketch, "E11.1.113.0", {"start": v(42.98, 1.4) * mm, "end": v(47.98, 1.5) * mm});
            skLineSegment(sketch, "E11.3.113.0", {"start": v(43, 0.4) * mm, "end": v(48, 0.5) * mm});
            skLineSegment(sketch, "E11.6.113.0", {"start": v(43, 0.9) * mm, "end": v(45.5, 0.95) * mm});
            skPoint(sketch, "E11.9.113.0", {"position": v(45.5, 0.95) * mm});
            skLineSegment(sketch, "E11.10.113.0", {"start": v(48, 0.5) * mm, "end": v(47.98, 1.5) * mm});
            skLineSegment(sketch, "E11.13.113.0", {"start": v(43, 0.4) * mm, "end": v(42.98, 1.4) * mm});
            skLineSegment(sketch, "E11.1.114.0", {"start": v(42.88, 3.2) * mm, "end": v(47.87, 3.51) * mm});
            skLineSegment(sketch, "E11.3.114.0", {"start": v(42.95, 2.2) * mm, "end": v(47.94, 2.51) * mm});
            skLineSegment(sketch, "E11.6.114.0", {"start": v(42.92, 2.7) * mm, "end": v(45.41, 2.86) * mm});
            skPoint(sketch, "E11.9.114.0", {"position": v(45.41, 2.86) * mm});
            skLineSegment(sketch, "E11.10.114.0", {"start": v(47.94, 2.51) * mm, "end": v(47.87, 3.51) * mm});
            skLineSegment(sketch, "E11.13.114.0", {"start": v(42.95, 2.2) * mm, "end": v(42.88, 3.2) * mm});
            skLineSegment(sketch, "E11.1.115.0", {"start": v(42.71, 5) * mm, "end": v(47.68, 5.51) * mm});
            skLineSegment(sketch, "E11.3.115.0", {"start": v(42.82, 4) * mm, "end": v(47.79, 4.52) * mm});
            skLineSegment(sketch, "E11.6.115.0", {"start": v(42.76, 4.5) * mm, "end": v(45.25, 4.76) * mm});
            skPoint(sketch, "E11.9.115.0", {"position": v(45.25, 4.76) * mm});
            skLineSegment(sketch, "E11.10.115.0", {"start": v(47.79, 4.52) * mm, "end": v(47.68, 5.51) * mm});
            skLineSegment(sketch, "E11.13.115.0", {"start": v(42.82, 4) * mm, "end": v(42.71, 5) * mm});
            skLineSegment(sketch, "E11.1.116.0", {"start": v(42.47, 6.78) * mm, "end": v(47.41, 7.5) * mm});
            skLineSegment(sketch, "E11.3.116.0", {"start": v(42.61, 5.79) * mm, "end": v(47.56, 6.52) * mm});
            skLineSegment(sketch, "E11.6.116.0", {"start": v(42.54, 6.28) * mm, "end": v(45.01, 6.65) * mm});
            skPoint(sketch, "E11.9.116.0", {"position": v(45.01, 6.65) * mm});
            skLineSegment(sketch, "E11.10.116.0", {"start": v(47.56, 6.52) * mm, "end": v(47.41, 7.5) * mm});
            skLineSegment(sketch, "E11.13.116.0", {"start": v(42.61, 5.79) * mm, "end": v(42.47, 6.78) * mm});
            skLineSegment(sketch, "E11.1.117.0", {"start": v(42.14, 8.55) * mm, "end": v(47.06, 9.49) * mm});
            skLineSegment(sketch, "E11.3.117.0", {"start": v(42.33, 7.57) * mm, "end": v(47.24, 8.5) * mm});
            skLineSegment(sketch, "E11.6.117.0", {"start": v(42.24, 8.06) * mm, "end": v(44.7, 8.53) * mm});
            skPoint(sketch, "E11.9.117.0", {"position": v(44.7, 8.53) * mm});
            skLineSegment(sketch, "E11.10.117.0", {"start": v(47.24, 8.5) * mm, "end": v(47.06, 9.49) * mm});
            skLineSegment(sketch, "E11.13.117.0", {"start": v(42.33, 7.57) * mm, "end": v(42.14, 8.55) * mm});
            skLineSegment(sketch, "E11.1.118.0", {"start": v(41.75, 10.3) * mm, "end": v(46.62, 11.45) * mm});
            skLineSegment(sketch, "E11.3.118.0", {"start": v(41.98, 9.33) * mm, "end": v(46.85, 10.47) * mm});
            skLineSegment(sketch, "E11.6.118.0", {"start": v(41.86, 9.82) * mm, "end": v(44.3, 10.39) * mm});
            skPoint(sketch, "E11.9.118.0", {"position": v(44.3, 10.39) * mm});
            skLineSegment(sketch, "E11.10.118.0", {"start": v(46.85, 10.47) * mm, "end": v(46.62, 11.45) * mm});
            skLineSegment(sketch, "E11.13.118.0", {"start": v(41.98, 9.33) * mm, "end": v(41.75, 10.3) * mm});
            skLineSegment(sketch, "E11.1.119.0", {"start": v(41.28, 12.05) * mm, "end": v(46.1, 13.39) * mm});
            skLineSegment(sketch, "E11.3.119.0", {"start": v(41.55, 11.08) * mm, "end": v(46.37, 12.43) * mm});
            skLineSegment(sketch, "E11.6.119.0", {"start": v(41.42, 11.56) * mm, "end": v(43.82, 12.24) * mm});
            skPoint(sketch, "E11.9.119.0", {"position": v(43.82, 12.24) * mm});
            skLineSegment(sketch, "E11.10.119.0", {"start": v(46.37, 12.43) * mm, "end": v(46.1, 13.39) * mm});
            skLineSegment(sketch, "E11.13.119.0", {"start": v(41.55, 11.08) * mm, "end": v(41.28, 12.05) * mm});
            skLineSegment(sketch, "E11.1.120.0", {"start": v(40.74, 13.76) * mm, "end": v(45.5, 15.3) * mm});
            skLineSegment(sketch, "E11.3.120.0", {"start": v(41.05, 12.81) * mm, "end": v(45.8, 14.36) * mm});
            skLineSegment(sketch, "E11.6.120.0", {"start": v(40.9, 13.29) * mm, "end": v(43.27, 14.06) * mm});
            skPoint(sketch, "E11.9.120.0", {"position": v(43.27, 14.06) * mm});
            skLineSegment(sketch, "E11.10.120.0", {"start": v(45.8, 14.36) * mm, "end": v(45.5, 15.3) * mm});
            skLineSegment(sketch, "E11.13.120.0", {"start": v(41.05, 12.81) * mm, "end": v(40.74, 13.76) * mm});
            skLineSegment(sketch, "E11.1.121.0", {"start": v(40.13, 15.46) * mm, "end": v(44.82, 17.2) * mm});
            skLineSegment(sketch, "E11.3.121.0", {"start": v(40.48, 14.52) * mm, "end": v(45.16, 16.26) * mm});
            skLineSegment(sketch, "E11.6.121.0", {"start": v(40.3, 14.99) * mm, "end": v(42.65, 15.86) * mm});
            skPoint(sketch, "E11.9.121.0", {"position": v(42.65, 15.86) * mm});
            skLineSegment(sketch, "E11.10.121.0", {"start": v(45.16, 16.26) * mm, "end": v(44.82, 17.2) * mm});
            skLineSegment(sketch, "E11.13.121.0", {"start": v(40.48, 14.52) * mm, "end": v(40.13, 15.46) * mm});
            skLineSegment(sketch, "E11.1.122.0", {"start": v(39.45, 17.12) * mm, "end": v(44.06, 19.06) * mm});
            skLineSegment(sketch, "E11.3.122.0", {"start": v(39.83, 16.2) * mm, "end": v(44.44, 18.14) * mm});
            skLineSegment(sketch, "E11.6.122.0", {"start": v(39.64, 16.66) * mm, "end": v(41.94, 17.63) * mm});
            skPoint(sketch, "E11.9.122.0", {"position": v(41.94, 17.63) * mm});
            skLineSegment(sketch, "E11.10.122.0", {"start": v(44.44, 18.14) * mm, "end": v(44.06, 19.06) * mm});
            skLineSegment(sketch, "E11.13.122.0", {"start": v(39.83, 16.2) * mm, "end": v(39.45, 17.12) * mm});
            skLineSegment(sketch, "E11.1.123.0", {"start": v(38.7, 18.76) * mm, "end": v(43.22, 20.89) * mm});
            skLineSegment(sketch, "E11.3.123.0", {"start": v(39.12, 17.86) * mm, "end": v(43.64, 19.98) * mm});
            skLineSegment(sketch, "E11.6.123.0", {"start": v(38.9, 18.3) * mm, "end": v(41.17, 19.37) * mm});
            skPoint(sketch, "E11.9.123.0", {"position": v(41.17, 19.37) * mm});
            skLineSegment(sketch, "E11.10.123.0", {"start": v(43.64, 19.98) * mm, "end": v(43.22, 20.89) * mm});
            skLineSegment(sketch, "E11.13.123.0", {"start": v(39.12, 17.86) * mm, "end": v(38.7, 18.76) * mm});
            skLineSegment(sketch, "E11.1.124.0", {"start": v(37.88, 20.36) * mm, "end": v(42.3, 22.68) * mm});
            skLineSegment(sketch, "E11.3.124.0", {"start": v(38.34, 19.48) * mm, "end": v(42.77, 21.8) * mm});
            skLineSegment(sketch, "E11.6.124.0", {"start": v(38.1, 19.92) * mm, "end": v(40.32, 21.08) * mm});
            skPoint(sketch, "E11.9.124.0", {"position": v(40.32, 21.08) * mm});
            skLineSegment(sketch, "E11.10.124.0", {"start": v(42.77, 21.8) * mm, "end": v(42.3, 22.68) * mm});
            skLineSegment(sketch, "E11.13.124.0", {"start": v(38.34, 19.48) * mm, "end": v(37.88, 20.36) * mm});
            skLineSegment(sketch, "E11.1.125.0", {"start": v(36.99, 21.93) * mm, "end": v(41.32, 24.43) * mm});
            skLineSegment(sketch, "E11.3.125.0", {"start": v(37.49, 21.07) * mm, "end": v(41.82, 23.57) * mm});
            skLineSegment(sketch, "E11.6.125.0", {"start": v(37.24, 21.5) * mm, "end": v(39.4, 22.75) * mm});
            skPoint(sketch, "E11.9.125.0", {"position": v(39.4, 22.75) * mm});
            skLineSegment(sketch, "E11.10.125.0", {"start": v(41.82, 23.57) * mm, "end": v(41.32, 24.43) * mm});
            skLineSegment(sketch, "E11.13.125.0", {"start": v(37.49, 21.07) * mm, "end": v(36.99, 21.93) * mm});
            skLineSegment(sketch, "E11.1.126.0", {"start": v(36.04, 23.46) * mm, "end": v(40.26, 26.14) * mm});
            skLineSegment(sketch, "E11.3.126.0", {"start": v(36.57, 22.62) * mm, "end": v(40.8, 25.3) * mm});
            skLineSegment(sketch, "E11.6.126.0", {"start": v(36.3, 23.04) * mm, "end": v(38.42, 24.38) * mm});
            skPoint(sketch, "E11.9.126.0", {"position": v(38.42, 24.38) * mm});
            skLineSegment(sketch, "E11.10.126.0", {"start": v(40.8, 25.3) * mm, "end": v(40.26, 26.14) * mm});
            skLineSegment(sketch, "E11.13.126.0", {"start": v(36.57, 22.62) * mm, "end": v(36.04, 23.46) * mm});
            skLineSegment(sketch, "E11.1.127.0", {"start": v(35.02, 24.95) * mm, "end": v(39.13, 27.8) * mm});
            skLineSegment(sketch, "E11.3.127.0", {"start": v(35.6, 24.13) * mm, "end": v(39.7, 26.98) * mm});
            skLineSegment(sketch, "E11.6.127.0", {"start": v(35.3, 24.54) * mm, "end": v(37.36, 25.97) * mm});
            skPoint(sketch, "E11.9.127.0", {"position": v(37.36, 25.97) * mm});
            skLineSegment(sketch, "E11.10.127.0", {"start": v(39.7, 26.98) * mm, "end": v(39.13, 27.8) * mm});
            skLineSegment(sketch, "E11.13.127.0", {"start": v(35.6, 24.13) * mm, "end": v(35.02, 24.95) * mm});
            skLineSegment(sketch, "E11.1.128.0", {"start": v(33.95, 26.4) * mm, "end": v(37.93, 29.42) * mm});
            skLineSegment(sketch, "E11.3.128.0", {"start": v(34.55, 25.6) * mm, "end": v(38.54, 28.62) * mm});
            skLineSegment(sketch, "E11.6.128.0", {"start": v(34.25, 26) * mm, "end": v(36.24, 27.5) * mm});
            skPoint(sketch, "E11.9.128.0", {"position": v(36.24, 27.5) * mm});
            skLineSegment(sketch, "E11.10.128.0", {"start": v(38.54, 28.62) * mm, "end": v(37.93, 29.42) * mm});
            skLineSegment(sketch, "E11.13.128.0", {"start": v(34.55, 25.6) * mm, "end": v(33.95, 26.4) * mm});
            skLineSegment(sketch, "E11.1.129.0", {"start": v(32.81, 27.8) * mm, "end": v(36.67, 30.98) * mm});
            skLineSegment(sketch, "E11.3.129.0", {"start": v(33.45, 27.02) * mm, "end": v(37.3, 30.21) * mm});
            skLineSegment(sketch, "E11.6.129.0", {"start": v(33.13, 27.4) * mm, "end": v(35.06, 29) * mm});
            skPoint(sketch, "E11.9.129.0", {"position": v(35.06, 29) * mm});
            skLineSegment(sketch, "E11.10.129.0", {"start": v(37.3, 30.21) * mm, "end": v(36.67, 30.98) * mm});
            skLineSegment(sketch, "E11.13.129.0", {"start": v(33.45, 27.02) * mm, "end": v(32.81, 27.8) * mm});
            skLineSegment(sketch, "E11.1.130.0", {"start": v(31.62, 29.14) * mm, "end": v(35.34, 32.49) * mm});
            skLineSegment(sketch, "E11.3.130.0", {"start": v(32.29, 28.4) * mm, "end": v(36, 31.75) * mm});
            skLineSegment(sketch, "E11.6.130.0", {"start": v(31.96, 28.77) * mm, "end": v(33.81, 30.45) * mm});
            skPoint(sketch, "E11.9.130.0", {"position": v(33.81, 30.45) * mm});
            skLineSegment(sketch, "E11.10.130.0", {"start": v(36, 31.75) * mm, "end": v(35.34, 32.49) * mm});
            skLineSegment(sketch, "E11.13.130.0", {"start": v(32.29, 28.4) * mm, "end": v(31.62, 29.14) * mm});
            skLineSegment(sketch, "E11.1.131.0", {"start": v(30.37, 30.44) * mm, "end": v(33.94, 33.94) * mm});
            skLineSegment(sketch, "E11.3.131.0", {"start": v(31.07, 29.73) * mm, "end": v(34.64, 33.23) * mm});
            skLineSegment(sketch, "E11.6.131.0", {"start": v(30.72, 30.09) * mm, "end": v(32.5, 31.83) * mm});
            skPoint(sketch, "E11.9.131.0", {"position": v(32.5, 31.83) * mm});
            skLineSegment(sketch, "E11.10.131.0", {"start": v(34.64, 33.23) * mm, "end": v(33.94, 33.94) * mm});
            skLineSegment(sketch, "E11.13.131.0", {"start": v(31.07, 29.73) * mm, "end": v(30.37, 30.44) * mm});
            skLineSegment(sketch, "E11.1.132.0", {"start": v(29.07, 31.69) * mm, "end": v(32.5, 35.33) * mm});
            skLineSegment(sketch, "E11.3.132.0", {"start": v(29.8, 31) * mm, "end": v(33.22, 34.65) * mm});
            skLineSegment(sketch, "E11.6.132.0", {"start": v(29.44, 31.35) * mm, "end": v(31.15, 33.17) * mm});
            skPoint(sketch, "E11.9.132.0", {"position": v(31.15, 33.17) * mm});
            skLineSegment(sketch, "E11.10.132.0", {"start": v(33.22, 34.65) * mm, "end": v(32.5, 35.33) * mm});
            skLineSegment(sketch, "E11.13.132.0", {"start": v(29.8, 31) * mm, "end": v(29.07, 31.69) * mm});
            skLineSegment(sketch, "E11.1.133.0", {"start": v(27.72, 32.88) * mm, "end": v(30.99, 36.66) * mm});
            skLineSegment(sketch, "E11.3.133.0", {"start": v(28.48, 32.22) * mm, "end": v(31.74, 36) * mm});
            skLineSegment(sketch, "E11.6.133.0", {"start": v(28.1, 32.55) * mm, "end": v(29.73, 34.44) * mm});
            skPoint(sketch, "E11.9.133.0", {"position": v(29.73, 34.44) * mm});
            skLineSegment(sketch, "E11.10.133.0", {"start": v(31.74, 36) * mm, "end": v(30.99, 36.66) * mm});
            skLineSegment(sketch, "E11.13.133.0", {"start": v(28.48, 32.22) * mm, "end": v(27.72, 32.88) * mm});
            skLineSegment(sketch, "E11.1.134.0", {"start": v(26.32, 34) * mm, "end": v(29.42, 37.93) * mm});
            skLineSegment(sketch, "E11.3.134.0", {"start": v(27.1, 33.39) * mm, "end": v(30.2, 37.3) * mm});
            skLineSegment(sketch, "E11.6.134.0", {"start": v(26.7, 33.7) * mm, "end": v(28.26, 35.66) * mm});
            skPoint(sketch, "E11.9.134.0", {"position": v(28.26, 35.66) * mm});
            skLineSegment(sketch, "E11.10.134.0", {"start": v(30.2, 37.3) * mm, "end": v(29.42, 37.93) * mm});
            skLineSegment(sketch, "E11.13.134.0", {"start": v(27.1, 33.39) * mm, "end": v(26.32, 34) * mm});
            skLineSegment(sketch, "E11.1.135.0", {"start": v(24.87, 35.08) * mm, "end": v(27.8, 39.13) * mm});
            skLineSegment(sketch, "E11.3.135.0", {"start": v(25.68, 34.5) * mm, "end": v(28.62, 38.54) * mm});
            skLineSegment(sketch, "E11.6.135.0", {"start": v(25.27, 34.79) * mm, "end": v(26.74, 36.81) * mm});
            skPoint(sketch, "E11.9.135.0", {"position": v(26.74, 36.81) * mm});
            skLineSegment(sketch, "E11.10.135.0", {"start": v(28.62, 38.54) * mm, "end": v(27.8, 39.13) * mm});
            skLineSegment(sketch, "E11.13.135.0", {"start": v(25.68, 34.5) * mm, "end": v(24.87, 35.08) * mm});
            skLineSegment(sketch, "E11.1.136.0", {"start": v(23.38, 36.1) * mm, "end": v(26.15, 40.26) * mm});
            skLineSegment(sketch, "E11.3.136.0", {"start": v(24.21, 35.54) * mm, "end": v(26.98, 39.7) * mm});
            skLineSegment(sketch, "E11.6.136.0", {"start": v(23.8, 35.82) * mm, "end": v(25.18, 37.9) * mm});
            skPoint(sketch, "E11.9.136.0", {"position": v(25.18, 37.9) * mm});
            skLineSegment(sketch, "E11.10.136.0", {"start": v(26.98, 39.7) * mm, "end": v(26.15, 40.26) * mm});
            skLineSegment(sketch, "E11.13.136.0", {"start": v(24.21, 35.54) * mm, "end": v(23.38, 36.1) * mm});
            skLineSegment(sketch, "E11.1.137.0", {"start": v(21.85, 37.04) * mm, "end": v(24.44, 41.32) * mm});
            skLineSegment(sketch, "E11.3.137.0", {"start": v(22.7, 36.52) * mm, "end": v(25.3, 40.8) * mm});
            skLineSegment(sketch, "E11.6.137.0", {"start": v(22.28, 36.78) * mm, "end": v(23.57, 38.92) * mm});
            skPoint(sketch, "E11.9.137.0", {"position": v(23.57, 38.92) * mm});
            skLineSegment(sketch, "E11.10.137.0", {"start": v(25.3, 40.8) * mm, "end": v(24.44, 41.32) * mm});
            skLineSegment(sketch, "E11.13.137.0", {"start": v(22.7, 36.52) * mm, "end": v(21.85, 37.04) * mm});
            skLineSegment(sketch, "E11.1.138.0", {"start": v(20.28, 37.92) * mm, "end": v(22.69, 42.3) * mm});
            skLineSegment(sketch, "E11.3.138.0", {"start": v(21.15, 37.44) * mm, "end": v(23.56, 41.82) * mm});
            skLineSegment(sketch, "E11.6.138.0", {"start": v(20.72, 37.68) * mm, "end": v(21.92, 39.87) * mm});
            skPoint(sketch, "E11.9.138.0", {"position": v(21.92, 39.87) * mm});
            skLineSegment(sketch, "E11.10.138.0", {"start": v(23.56, 41.82) * mm, "end": v(22.69, 42.3) * mm});
            skLineSegment(sketch, "E11.13.138.0", {"start": v(21.15, 37.44) * mm, "end": v(20.28, 37.92) * mm});
            skLineSegment(sketch, "E11.1.139.0", {"start": v(18.67, 38.74) * mm, "end": v(20.9, 43.22) * mm});
            skLineSegment(sketch, "E11.3.139.0", {"start": v(19.57, 38.3) * mm, "end": v(21.8, 42.77) * mm});
            skLineSegment(sketch, "E11.6.139.0", {"start": v(19.12, 38.52) * mm, "end": v(20.23, 40.75) * mm});
            skPoint(sketch, "E11.9.139.0", {"position": v(20.23, 40.75) * mm});
            skLineSegment(sketch, "E11.10.139.0", {"start": v(21.8, 42.77) * mm, "end": v(20.9, 43.22) * mm});
            skLineSegment(sketch, "E11.13.139.0", {"start": v(19.57, 38.3) * mm, "end": v(18.67, 38.74) * mm});
            skLineSegment(sketch, "E11.1.140.0", {"start": v(17.03, 39.49) * mm, "end": v(19.07, 44.05) * mm});
            skLineSegment(sketch, "E11.3.140.0", {"start": v(17.95, 39.08) * mm, "end": v(19.98, 43.65) * mm});
            skLineSegment(sketch, "E11.6.140.0", {"start": v(17.49, 39.28) * mm, "end": v(18.5, 41.57) * mm});
            skPoint(sketch, "E11.9.140.0", {"position": v(18.5, 41.57) * mm});
            skLineSegment(sketch, "E11.10.140.0", {"start": v(19.98, 43.65) * mm, "end": v(19.07, 44.05) * mm});
            skLineSegment(sketch, "E11.13.140.0", {"start": v(17.95, 39.08) * mm, "end": v(17.03, 39.49) * mm});
            skLineSegment(sketch, "E11.1.141.0", {"start": v(15.36, 40.16) * mm, "end": v(17.2, 44.81) * mm});
            skLineSegment(sketch, "E11.3.141.0", {"start": v(16.3, 39.8) * mm, "end": v(18.13, 44.45) * mm});
            skLineSegment(sketch, "E11.6.141.0", {"start": v(15.83, 39.98) * mm, "end": v(16.75, 42.3) * mm});
            skPoint(sketch, "E11.9.141.0", {"position": v(16.75, 42.3) * mm});
            skLineSegment(sketch, "E11.10.141.0", {"start": v(18.13, 44.45) * mm, "end": v(17.2, 44.81) * mm});
            skLineSegment(sketch, "E11.13.141.0", {"start": v(16.3, 39.8) * mm, "end": v(15.36, 40.16) * mm});
            skLineSegment(sketch, "E11.1.142.0", {"start": v(13.67, 40.77) * mm, "end": v(15.31, 45.5) * mm});
            skLineSegment(sketch, "E11.3.142.0", {"start": v(14.61, 40.44) * mm, "end": v(16.26, 45.17) * mm});
            skLineSegment(sketch, "E11.6.142.0", {"start": v(14.14, 40.6) * mm, "end": v(14.96, 42.97) * mm});
            skPoint(sketch, "E11.9.142.0", {"position": v(14.96, 42.97) * mm});
            skLineSegment(sketch, "E11.10.142.0", {"start": v(16.26, 45.17) * mm, "end": v(15.31, 45.5) * mm});
            skLineSegment(sketch, "E11.13.142.0", {"start": v(14.61, 40.44) * mm, "end": v(13.67, 40.77) * mm});
            skLineSegment(sketch, "E11.1.143.0", {"start": v(11.95, 41.3) * mm, "end": v(13.4, 46.1) * mm});
            skLineSegment(sketch, "E11.3.143.0", {"start": v(12.9, 41.02) * mm, "end": v(14.35, 45.8) * mm});
            skLineSegment(sketch, "E11.6.143.0", {"start": v(12.43, 41.16) * mm, "end": v(13.15, 43.56) * mm});
            skPoint(sketch, "E11.9.143.0", {"position": v(13.15, 43.56) * mm});
            skLineSegment(sketch, "E11.10.143.0", {"start": v(14.35, 45.8) * mm, "end": v(13.4, 46.1) * mm});
            skLineSegment(sketch, "E11.13.143.0", {"start": v(12.9, 41.02) * mm, "end": v(11.95, 41.3) * mm});
            skLineSegment(sketch, "E11.1.144.0", {"start": v(10.2, 41.77) * mm, "end": v(11.45, 46.62) * mm});
            skLineSegment(sketch, "E11.3.144.0", {"start": v(11.18, 41.52) * mm, "end": v(12.42, 46.37) * mm});
            skLineSegment(sketch, "E11.6.144.0", {"start": v(10.7, 41.65) * mm, "end": v(11.32, 44.07) * mm});
            skPoint(sketch, "E11.9.144.0", {"position": v(11.32, 44.07) * mm});
            skLineSegment(sketch, "E11.10.144.0", {"start": v(12.42, 46.37) * mm, "end": v(11.45, 46.62) * mm});
            skLineSegment(sketch, "E11.13.144.0", {"start": v(11.18, 41.52) * mm, "end": v(10.2, 41.77) * mm});
            skLineSegment(sketch, "E11.1.145.0", {"start": v(8.45, 42.16) * mm, "end": v(9.5, 47.06) * mm});
            skLineSegment(sketch, "E11.3.145.0", {"start": v(9.43, 41.96) * mm, "end": v(10.47, 46.85) * mm});
            skLineSegment(sketch, "E11.6.145.0", {"start": v(8.94, 42.06) * mm, "end": v(9.46, 44.5) * mm});
            skPoint(sketch, "E11.9.145.0", {"position": v(9.46, 44.5) * mm});
            skLineSegment(sketch, "E11.10.145.0", {"start": v(10.47, 46.85) * mm, "end": v(9.5, 47.06) * mm});
            skLineSegment(sketch, "E11.13.145.0", {"start": v(9.43, 41.96) * mm, "end": v(8.45, 42.16) * mm});
            skLineSegment(sketch, "E11.1.146.0", {"start": v(6.68, 42.48) * mm, "end": v(7.51, 47.41) * mm});
            skLineSegment(sketch, "E11.3.146.0", {"start": v(7.66, 42.31) * mm, "end": v(8.5, 47.24) * mm});
            skLineSegment(sketch, "E11.6.146.0", {"start": v(7.17, 42.4) * mm, "end": v(7.59, 44.86) * mm});
            skPoint(sketch, "E11.9.146.0", {"position": v(7.59, 44.86) * mm});
            skLineSegment(sketch, "E11.10.146.0", {"start": v(8.5, 47.24) * mm, "end": v(7.51, 47.41) * mm});
            skLineSegment(sketch, "E11.13.146.0", {"start": v(7.66, 42.31) * mm, "end": v(6.68, 42.48) * mm});
            skLineSegment(sketch, "E11.1.147.0", {"start": v(4.9, 42.72) * mm, "end": v(5.52, 47.68) * mm});
            skLineSegment(sketch, "E11.3.147.0", {"start": v(5.89, 42.6) * mm, "end": v(6.51, 47.56) * mm});
            skLineSegment(sketch, "E11.6.147.0", {"start": v(5.39, 42.66) * mm, "end": v(5.7, 45.14) * mm});
            skPoint(sketch, "E11.9.147.0", {"position": v(5.7, 45.14) * mm});
            skLineSegment(sketch, "E11.10.147.0", {"start": v(6.51, 47.56) * mm, "end": v(5.52, 47.68) * mm});
            skLineSegment(sketch, "E11.13.147.0", {"start": v(5.89, 42.6) * mm, "end": v(4.9, 42.72) * mm});
            skLineSegment(sketch, "E11.1.148.0", {"start": v(3.1, 42.9) * mm, "end": v(3.52, 47.87) * mm});
            skLineSegment(sketch, "E11.3.148.0", {"start": v(4.1, 42.8) * mm, "end": v(4.51, 47.79) * mm});
            skLineSegment(sketch, "E11.6.148.0", {"start": v(3.6, 42.85) * mm, "end": v(3.8, 45.34) * mm});
            skPoint(sketch, "E11.9.148.0", {"position": v(3.8, 45.34) * mm});
            skLineSegment(sketch, "E11.10.148.0", {"start": v(4.51, 47.79) * mm, "end": v(3.52, 47.87) * mm});
            skLineSegment(sketch, "E11.13.148.0", {"start": v(4.1, 42.8) * mm, "end": v(3.1, 42.9) * mm});
            skLineSegment(sketch, "E11.1.149.0", {"start": v(1.3, 42.98) * mm, "end": v(1.51, 47.98) * mm});
            skLineSegment(sketch, "E11.3.149.0", {"start": v(2.3, 42.94) * mm, "end": v(2.5, 47.94) * mm});
            skLineSegment(sketch, "E11.6.149.0", {"start": v(1.8, 42.96) * mm, "end": v(1.9, 45.46) * mm});
            skPoint(sketch, "E11.9.149.0", {"position": v(1.9, 45.46) * mm});
            skLineSegment(sketch, "E11.10.149.0", {"start": v(2.5, 47.94) * mm, "end": v(1.51, 47.98) * mm});
            skLineSegment(sketch, "E11.13.149.0", {"start": v(2.3, 42.94) * mm, "end": v(1.3, 42.98) * mm});
            skSolve(sketch);
        }
        {
            var Q0;
            Q0=makeQuery(id+"F0.imprint","IMPRINT",FACE,{"disambiguationData":[TD([[makeQuery(id+"F0.imprint","IMPRINT",EDGE,{"derivedFrom":sQuery(id+"F0.wireOp",EDGE,"E0")}),1.0]])]});
            extrude(context, id + "F1", {"entities" : qUnion([Q0]), "depth" : 3 * mm});
        }
    });
